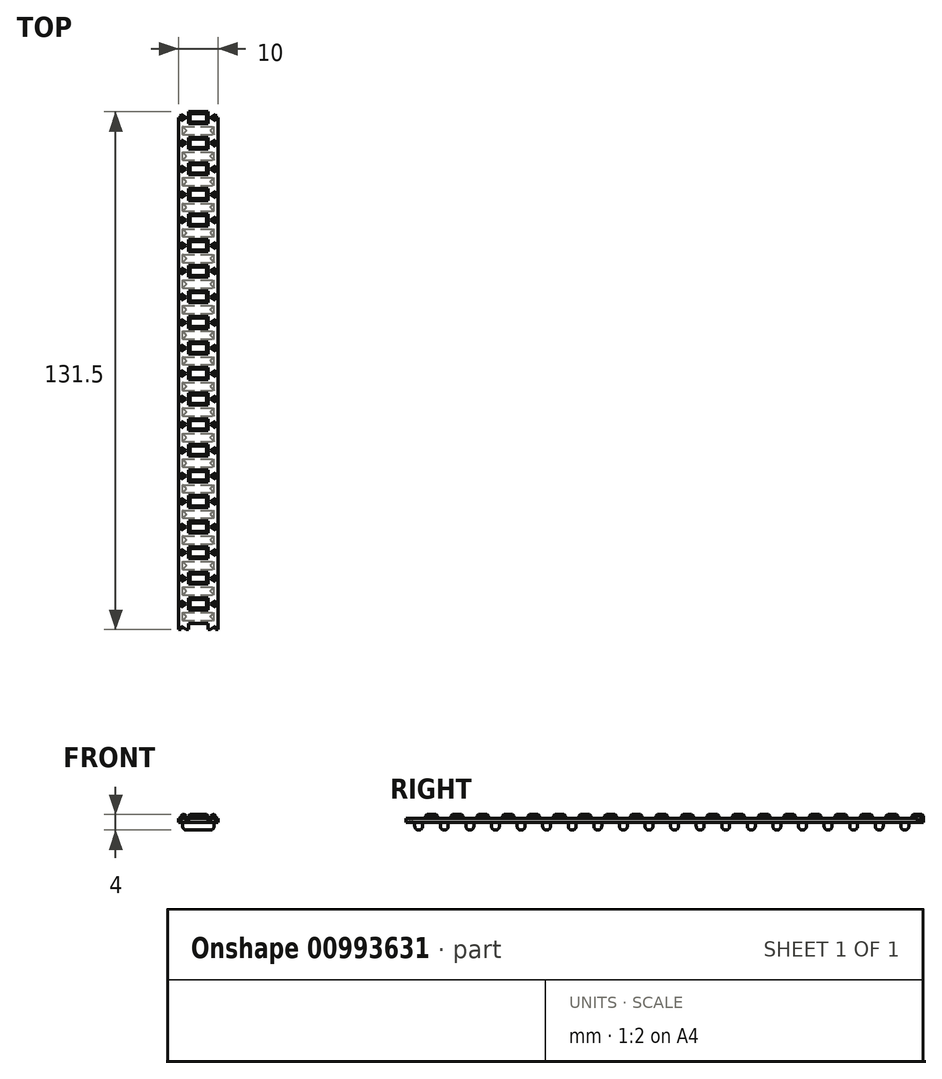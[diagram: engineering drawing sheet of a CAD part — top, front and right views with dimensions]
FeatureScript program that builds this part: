
annotation { "Feature Type Name" : "Feature", "Feature Type Description" : "" }
export const myFeature = defineFeature(function(context is Context, id is Id, definition is map)
    precondition{}
    {
        {
            var Q0;
            Q0=qCreatedBy(makeId("Top.planeOp"),FACE);
            var sketch = newSketch(context, id + "F0", { "sketchPlane" : qUnion([Q0])});
            skLineSegment(sketch, "E0.bottom", {"start": v(5, 65) * mm, "end": v(-5, 65) * mm});
            skLineSegment(sketch, "E0.top", {"start": v(5, -65) * mm, "end": v(-5, -65) * mm});
            skLineSegment(sketch, "E0.left", {"start": v(5, 65) * mm, "end": v(5, -65) * mm});
            skLineSegment(sketch, "E0.right", {"start": v(-5, 65) * mm, "end": v(-5, -65) * mm});
            skPoint(sketch, "E0.middle", {"position": v(0, 0) * mm});
            skLineSegment(sketch, "E1.bottom", {"start": v(2.5, 1.5) * mm, "end": v(-2.5, 1.5) * mm});
            skLineSegment(sketch, "E1.top", {"start": v(2.5, -1.5) * mm, "end": v(-2.5, -1.5) * mm});
            skLineSegment(sketch, "E1.left", {"start": v(2.5, 1.5) * mm, "end": v(2.5, -1.5) * mm});
            skLineSegment(sketch, "E1.right", {"start": v(-2.5, 1.5) * mm, "end": v(-2.5, -1.5) * mm});
            skLineSegment(sketch, "E2", {"start": v(3.08, 0) * mm, "end": v(4.42, 0.87) * mm});
            skLineSegment(sketch, "E3", {"start": v(4.42, 0.87) * mm, "end": v(4.42, 0) * mm});
            skLineSegment(sketch, "E4", {"start": v(4.42, 0) * mm, "end": v(3.08, 0) * mm});
            skLineSegment(sketch, "E5", {"start": v(3.08, 0) * mm, "end": v(4.42, -0.87) * mm});
            skLineSegment(sketch, "E6", {"start": v(4.42, -0.87) * mm, "end": v(4.42, 0) * mm});
            skLineSegment(sketch, "E7", {"start": v(4.42, 0) * mm, "end": v(5, 0) * mm});
            skLineSegment(sketch, "E8", {"start": v(3.08, 0) * mm, "end": v(2.5, 0) * mm});
            skLineSegment(sketch, "E9.MirrorCS", {"start": v(-3.08, 0) * mm, "end": v(-4.42, 0.87) * mm});
            skLineSegment(sketch, "E10.MirrorCS", {"start": v(-3.08, 0) * mm, "end": v(-4.42, -0.87) * mm});
            skLineSegment(sketch, "E11.MirrorCS", {"start": v(-4.42, -0.87) * mm, "end": v(-4.42, 0) * mm});
            skLineSegment(sketch, "E12.MirrorCS", {"start": v(-4.42, 0.87) * mm, "end": v(-4.42, 0) * mm});
            skLineSegment(sketch, "E13.0.1.0", {"start": v(3.08, 6.5) * mm, "end": v(4.42, 7.37) * mm});
            skLineSegment(sketch, "E13.0.1.1", {"start": v(4.42, 7.37) * mm, "end": v(4.42, 6.5) * mm});
            skLineSegment(sketch, "E13.0.1.2", {"start": v(4.42, 5.63) * mm, "end": v(4.42, 6.5) * mm});
            skLineSegment(sketch, "E13.0.1.3", {"start": v(3.08, 6.5) * mm, "end": v(4.42, 5.63) * mm});
            skLineSegment(sketch, "E13.0.1.4", {"start": v(-4.42, 7.37) * mm, "end": v(-4.42, 6.5) * mm});
            skLineSegment(sketch, "E13.0.1.5", {"start": v(-3.08, 6.5) * mm, "end": v(-4.42, 7.37) * mm});
            skLineSegment(sketch, "E13.0.1.6", {"start": v(-3.08, 6.5) * mm, "end": v(-4.42, 5.63) * mm});
            skLineSegment(sketch, "E13.0.1.7", {"start": v(-4.42, 5.63) * mm, "end": v(-4.42, 6.5) * mm});
            skLineSegment(sketch, "E13.0.1.8", {"start": v(2.5, 8) * mm, "end": v(-2.5, 8) * mm});
            skLineSegment(sketch, "E13.0.1.9", {"start": v(-2.5, 8) * mm, "end": v(-2.5, 5) * mm});
            skLineSegment(sketch, "E13.0.1.10", {"start": v(2.5, 5) * mm, "end": v(-2.5, 5) * mm});
            skLineSegment(sketch, "E13.0.1.11", {"start": v(2.5, 8) * mm, "end": v(2.5, 5) * mm});
            skLineSegment(sketch, "E13.0.2.0", {"start": v(3.08, 13) * mm, "end": v(4.42, 13.87) * mm});
            skLineSegment(sketch, "E13.0.2.1", {"start": v(4.42, 13.87) * mm, "end": v(4.42, 13) * mm});
            skLineSegment(sketch, "E13.0.2.2", {"start": v(4.42, 12.13) * mm, "end": v(4.42, 13) * mm});
            skLineSegment(sketch, "E13.0.2.3", {"start": v(3.08, 13) * mm, "end": v(4.42, 12.13) * mm});
            skLineSegment(sketch, "E13.0.2.4", {"start": v(-4.42, 13.87) * mm, "end": v(-4.42, 13) * mm});
            skLineSegment(sketch, "E13.0.2.5", {"start": v(-3.08, 13) * mm, "end": v(-4.42, 13.87) * mm});
            skLineSegment(sketch, "E13.0.2.6", {"start": v(-3.08, 13) * mm, "end": v(-4.42, 12.13) * mm});
            skLineSegment(sketch, "E13.0.2.7", {"start": v(-4.42, 12.13) * mm, "end": v(-4.42, 13) * mm});
            skLineSegment(sketch, "E13.0.2.8", {"start": v(2.5, 14.5) * mm, "end": v(-2.5, 14.5) * mm});
            skLineSegment(sketch, "E13.0.2.9", {"start": v(-2.5, 14.5) * mm, "end": v(-2.5, 11.5) * mm});
            skLineSegment(sketch, "E13.0.2.10", {"start": v(2.5, 11.5) * mm, "end": v(-2.5, 11.5) * mm});
            skLineSegment(sketch, "E13.0.2.11", {"start": v(2.5, 14.5) * mm, "end": v(2.5, 11.5) * mm});
            skLineSegment(sketch, "E13.0.3.0", {"start": v(3.08, 19.5) * mm, "end": v(4.42, 20.37) * mm});
            skLineSegment(sketch, "E13.0.3.1", {"start": v(4.42, 20.37) * mm, "end": v(4.42, 19.5) * mm});
            skLineSegment(sketch, "E13.0.3.2", {"start": v(4.42, 18.63) * mm, "end": v(4.42, 19.5) * mm});
            skLineSegment(sketch, "E13.0.3.3", {"start": v(3.08, 19.5) * mm, "end": v(4.42, 18.63) * mm});
            skLineSegment(sketch, "E13.0.3.4", {"start": v(-4.42, 20.37) * mm, "end": v(-4.42, 19.5) * mm});
            skLineSegment(sketch, "E13.0.3.5", {"start": v(-3.08, 19.5) * mm, "end": v(-4.42, 20.37) * mm});
            skLineSegment(sketch, "E13.0.3.6", {"start": v(-3.08, 19.5) * mm, "end": v(-4.42, 18.63) * mm});
            skLineSegment(sketch, "E13.0.3.7", {"start": v(-4.42, 18.63) * mm, "end": v(-4.42, 19.5) * mm});
            skLineSegment(sketch, "E13.0.3.8", {"start": v(2.5, 21) * mm, "end": v(-2.5, 21) * mm});
            skLineSegment(sketch, "E13.0.3.9", {"start": v(-2.5, 21) * mm, "end": v(-2.5, 18) * mm});
            skLineSegment(sketch, "E13.0.3.10", {"start": v(2.5, 18) * mm, "end": v(-2.5, 18) * mm});
            skLineSegment(sketch, "E13.0.3.11", {"start": v(2.5, 21) * mm, "end": v(2.5, 18) * mm});
            skLineSegment(sketch, "E13.0.4.0", {"start": v(3.08, 26) * mm, "end": v(4.42, 26.87) * mm});
            skLineSegment(sketch, "E13.0.4.1", {"start": v(4.42, 26.87) * mm, "end": v(4.42, 26) * mm});
            skLineSegment(sketch, "E13.0.4.2", {"start": v(4.42, 25.13) * mm, "end": v(4.42, 26) * mm});
            skLineSegment(sketch, "E13.0.4.3", {"start": v(3.08, 26) * mm, "end": v(4.42, 25.13) * mm});
            skLineSegment(sketch, "E13.0.4.4", {"start": v(-4.42, 26.87) * mm, "end": v(-4.42, 26) * mm});
            skLineSegment(sketch, "E13.0.4.5", {"start": v(-3.08, 26) * mm, "end": v(-4.42, 26.87) * mm});
            skLineSegment(sketch, "E13.0.4.6", {"start": v(-3.08, 26) * mm, "end": v(-4.42, 25.13) * mm});
            skLineSegment(sketch, "E13.0.4.7", {"start": v(-4.42, 25.13) * mm, "end": v(-4.42, 26) * mm});
            skLineSegment(sketch, "E13.0.4.8", {"start": v(2.5, 27.5) * mm, "end": v(-2.5, 27.5) * mm});
            skLineSegment(sketch, "E13.0.4.9", {"start": v(-2.5, 27.5) * mm, "end": v(-2.5, 24.5) * mm});
            skLineSegment(sketch, "E13.0.4.10", {"start": v(2.5, 24.5) * mm, "end": v(-2.5, 24.5) * mm});
            skLineSegment(sketch, "E13.0.4.11", {"start": v(2.5, 27.5) * mm, "end": v(2.5, 24.5) * mm});
            skLineSegment(sketch, "E13.0.5.0", {"start": v(3.08, 32.5) * mm, "end": v(4.42, 33.37) * mm});
            skLineSegment(sketch, "E13.0.5.1", {"start": v(4.42, 33.37) * mm, "end": v(4.42, 32.5) * mm});
            skLineSegment(sketch, "E13.0.5.2", {"start": v(4.42, 31.63) * mm, "end": v(4.42, 32.5) * mm});
            skLineSegment(sketch, "E13.0.5.3", {"start": v(3.08, 32.5) * mm, "end": v(4.42, 31.63) * mm});
            skLineSegment(sketch, "E13.0.5.4", {"start": v(-4.42, 33.37) * mm, "end": v(-4.42, 32.5) * mm});
            skLineSegment(sketch, "E13.0.5.5", {"start": v(-3.08, 32.5) * mm, "end": v(-4.42, 33.37) * mm});
            skLineSegment(sketch, "E13.0.5.6", {"start": v(-3.08, 32.5) * mm, "end": v(-4.42, 31.63) * mm});
            skLineSegment(sketch, "E13.0.5.7", {"start": v(-4.42, 31.63) * mm, "end": v(-4.42, 32.5) * mm});
            skLineSegment(sketch, "E13.0.5.8", {"start": v(2.5, 34) * mm, "end": v(-2.5, 34) * mm});
            skLineSegment(sketch, "E13.0.5.9", {"start": v(-2.5, 34) * mm, "end": v(-2.5, 31) * mm});
            skLineSegment(sketch, "E13.0.5.10", {"start": v(2.5, 31) * mm, "end": v(-2.5, 31) * mm});
            skLineSegment(sketch, "E13.0.5.11", {"start": v(2.5, 34) * mm, "end": v(2.5, 31) * mm});
            skLineSegment(sketch, "E13.0.6.0", {"start": v(3.08, 39) * mm, "end": v(4.42, 39.87) * mm});
            skLineSegment(sketch, "E13.0.6.1", {"start": v(4.42, 39.87) * mm, "end": v(4.42, 39) * mm});
            skLineSegment(sketch, "E13.0.6.2", {"start": v(4.42, 38.13) * mm, "end": v(4.42, 39) * mm});
            skLineSegment(sketch, "E13.0.6.3", {"start": v(3.08, 39) * mm, "end": v(4.42, 38.13) * mm});
            skLineSegment(sketch, "E13.0.6.4", {"start": v(-4.42, 39.87) * mm, "end": v(-4.42, 39) * mm});
            skLineSegment(sketch, "E13.0.6.5", {"start": v(-3.08, 39) * mm, "end": v(-4.42, 39.87) * mm});
            skLineSegment(sketch, "E13.0.6.6", {"start": v(-3.08, 39) * mm, "end": v(-4.42, 38.13) * mm});
            skLineSegment(sketch, "E13.0.6.7", {"start": v(-4.42, 38.13) * mm, "end": v(-4.42, 39) * mm});
            skLineSegment(sketch, "E13.0.6.8", {"start": v(2.5, 40.5) * mm, "end": v(-2.5, 40.5) * mm});
            skLineSegment(sketch, "E13.0.6.9", {"start": v(-2.5, 40.5) * mm, "end": v(-2.5, 37.5) * mm});
            skLineSegment(sketch, "E13.0.6.10", {"start": v(2.5, 37.5) * mm, "end": v(-2.5, 37.5) * mm});
            skLineSegment(sketch, "E13.0.6.11", {"start": v(2.5, 40.5) * mm, "end": v(2.5, 37.5) * mm});
            skLineSegment(sketch, "E13.0.7.0", {"start": v(3.08, 45.5) * mm, "end": v(4.42, 46.37) * mm});
            skLineSegment(sketch, "E13.0.7.1", {"start": v(4.42, 46.37) * mm, "end": v(4.42, 45.5) * mm});
            skLineSegment(sketch, "E13.0.7.2", {"start": v(4.42, 44.63) * mm, "end": v(4.42, 45.5) * mm});
            skLineSegment(sketch, "E13.0.7.3", {"start": v(3.08, 45.5) * mm, "end": v(4.42, 44.63) * mm});
            skLineSegment(sketch, "E13.0.7.4", {"start": v(-4.42, 46.37) * mm, "end": v(-4.42, 45.5) * mm});
            skLineSegment(sketch, "E13.0.7.5", {"start": v(-3.08, 45.5) * mm, "end": v(-4.42, 46.37) * mm});
            skLineSegment(sketch, "E13.0.7.6", {"start": v(-3.08, 45.5) * mm, "end": v(-4.42, 44.63) * mm});
            skLineSegment(sketch, "E13.0.7.7", {"start": v(-4.42, 44.63) * mm, "end": v(-4.42, 45.5) * mm});
            skLineSegment(sketch, "E13.0.7.8", {"start": v(2.5, 47) * mm, "end": v(-2.5, 47) * mm});
            skLineSegment(sketch, "E13.0.7.9", {"start": v(-2.5, 47) * mm, "end": v(-2.5, 44) * mm});
            skLineSegment(sketch, "E13.0.7.10", {"start": v(2.5, 44) * mm, "end": v(-2.5, 44) * mm});
            skLineSegment(sketch, "E13.0.7.11", {"start": v(2.5, 47) * mm, "end": v(2.5, 44) * mm});
            skLineSegment(sketch, "E13.0.8.0", {"start": v(3.08, 52) * mm, "end": v(4.42, 52.87) * mm});
            skLineSegment(sketch, "E13.0.8.1", {"start": v(4.42, 52.87) * mm, "end": v(4.42, 52) * mm});
            skLineSegment(sketch, "E13.0.8.2", {"start": v(4.42, 51.13) * mm, "end": v(4.42, 52) * mm});
            skLineSegment(sketch, "E13.0.8.3", {"start": v(3.08, 52) * mm, "end": v(4.42, 51.13) * mm});
            skLineSegment(sketch, "E13.0.8.4", {"start": v(-4.42, 52.87) * mm, "end": v(-4.42, 52) * mm});
            skLineSegment(sketch, "E13.0.8.5", {"start": v(-3.08, 52) * mm, "end": v(-4.42, 52.87) * mm});
            skLineSegment(sketch, "E13.0.8.6", {"start": v(-3.08, 52) * mm, "end": v(-4.42, 51.13) * mm});
            skLineSegment(sketch, "E13.0.8.7", {"start": v(-4.42, 51.13) * mm, "end": v(-4.42, 52) * mm});
            skLineSegment(sketch, "E13.0.8.8", {"start": v(2.5, 53.5) * mm, "end": v(-2.5, 53.5) * mm});
            skLineSegment(sketch, "E13.0.8.9", {"start": v(-2.5, 53.5) * mm, "end": v(-2.5, 50.5) * mm});
            skLineSegment(sketch, "E13.0.8.10", {"start": v(2.5, 50.5) * mm, "end": v(-2.5, 50.5) * mm});
            skLineSegment(sketch, "E13.0.8.11", {"start": v(2.5, 53.5) * mm, "end": v(2.5, 50.5) * mm});
            skLineSegment(sketch, "E13.0.9.0", {"start": v(3.08, 58.5) * mm, "end": v(4.42, 59.37) * mm});
            skLineSegment(sketch, "E13.0.9.1", {"start": v(4.42, 59.37) * mm, "end": v(4.42, 58.5) * mm});
            skLineSegment(sketch, "E13.0.9.2", {"start": v(4.42, 57.63) * mm, "end": v(4.42, 58.5) * mm});
            skLineSegment(sketch, "E13.0.9.3", {"start": v(3.08, 58.5) * mm, "end": v(4.42, 57.63) * mm});
            skLineSegment(sketch, "E13.0.9.4", {"start": v(-4.42, 59.37) * mm, "end": v(-4.42, 58.5) * mm});
            skLineSegment(sketch, "E13.0.9.5", {"start": v(-3.08, 58.5) * mm, "end": v(-4.42, 59.37) * mm});
            skLineSegment(sketch, "E13.0.9.6", {"start": v(-3.08, 58.5) * mm, "end": v(-4.42, 57.63) * mm});
            skLineSegment(sketch, "E13.0.9.7", {"start": v(-4.42, 57.63) * mm, "end": v(-4.42, 58.5) * mm});
            skLineSegment(sketch, "E13.0.9.8", {"start": v(2.5, 60) * mm, "end": v(-2.5, 60) * mm});
            skLineSegment(sketch, "E13.0.9.9", {"start": v(-2.5, 60) * mm, "end": v(-2.5, 57) * mm});
            skLineSegment(sketch, "E13.0.9.10", {"start": v(2.5, 57) * mm, "end": v(-2.5, 57) * mm});
            skLineSegment(sketch, "E13.0.9.11", {"start": v(2.5, 60) * mm, "end": v(2.5, 57) * mm});
            skLineSegment(sketch, "E13.0.10.0", {"start": v(3.08, 65) * mm, "end": v(4.42, 65.87) * mm});
            skLineSegment(sketch, "E13.0.10.1", {"start": v(4.42, 65.87) * mm, "end": v(4.42, 65) * mm});
            skLineSegment(sketch, "E13.0.10.2", {"start": v(4.42, 64.13) * mm, "end": v(4.42, 65) * mm});
            skLineSegment(sketch, "E13.0.10.3", {"start": v(3.08, 65) * mm, "end": v(4.42, 64.13) * mm});
            skLineSegment(sketch, "E13.0.10.4", {"start": v(-4.42, 65.87) * mm, "end": v(-4.42, 65) * mm});
            skLineSegment(sketch, "E13.0.10.5", {"start": v(-3.08, 65) * mm, "end": v(-4.42, 65.87) * mm});
            skLineSegment(sketch, "E13.0.10.6", {"start": v(-3.08, 65) * mm, "end": v(-4.42, 64.13) * mm});
            skLineSegment(sketch, "E13.0.10.7", {"start": v(-4.42, 64.13) * mm, "end": v(-4.42, 65) * mm});
            skLineSegment(sketch, "E13.0.10.8", {"start": v(2.5, 66.5) * mm, "end": v(-2.5, 66.5) * mm});
            skLineSegment(sketch, "E13.0.10.9", {"start": v(-2.5, 66.5) * mm, "end": v(-2.5, 63.5) * mm});
            skLineSegment(sketch, "E13.0.10.10", {"start": v(2.5, 63.5) * mm, "end": v(-2.5, 63.5) * mm});
            skLineSegment(sketch, "E13.0.10.11", {"start": v(2.5, 66.5) * mm, "end": v(2.5, 63.5) * mm});
            skLineSegment(sketch, "E13.direction1", {"start": v(3.08, 0) * mm, "end": v(20.08, 0) * mm, "construction": true});
            skLineSegment(sketch, "E13.direction2", {"start": v(3.08, 0) * mm, "end": v(3.08, 6.5) * mm, "construction": true});
            skLineSegment(sketch, "E14.0.1.0", {"start": v(-3.08, -6.5) * mm, "end": v(-4.42, -5.63) * mm});
            skLineSegment(sketch, "E14.0.1.1", {"start": v(-4.42, -5.63) * mm, "end": v(-4.42, -6.5) * mm});
            skLineSegment(sketch, "E14.0.1.2", {"start": v(-4.42, -7.37) * mm, "end": v(-4.42, -6.5) * mm});
            skLineSegment(sketch, "E14.0.1.3", {"start": v(-3.08, -6.5) * mm, "end": v(-4.42, -7.37) * mm});
            skLineSegment(sketch, "E14.0.1.4", {"start": v(-2.5, -5) * mm, "end": v(-2.5, -8) * mm});
            skLineSegment(sketch, "E14.0.1.5", {"start": v(2.5, -5) * mm, "end": v(-2.5, -5) * mm});
            skLineSegment(sketch, "E14.0.1.6", {"start": v(2.5, -5) * mm, "end": v(2.5, -8) * mm});
            skLineSegment(sketch, "E14.0.1.7", {"start": v(2.5, -8) * mm, "end": v(-2.5, -8) * mm});
            skLineSegment(sketch, "E14.0.1.8", {"start": v(3.08, -6.5) * mm, "end": v(4.42, -7.37) * mm});
            skLineSegment(sketch, "E14.0.1.9", {"start": v(3.08, -6.5) * mm, "end": v(4.42, -5.63) * mm});
            skLineSegment(sketch, "E14.0.1.10", {"start": v(4.42, -5.63) * mm, "end": v(4.42, -6.5) * mm});
            skLineSegment(sketch, "E14.0.1.11", {"start": v(4.42, -7.37) * mm, "end": v(4.42, -6.5) * mm});
            skLineSegment(sketch, "E14.0.2.0", {"start": v(-3.08, -13) * mm, "end": v(-4.42, -12.13) * mm});
            skLineSegment(sketch, "E14.0.2.1", {"start": v(-4.42, -12.13) * mm, "end": v(-4.42, -13) * mm});
            skLineSegment(sketch, "E14.0.2.2", {"start": v(-4.42, -13.87) * mm, "end": v(-4.42, -13) * mm});
            skLineSegment(sketch, "E14.0.2.3", {"start": v(-3.08, -13) * mm, "end": v(-4.42, -13.87) * mm});
            skLineSegment(sketch, "E14.0.2.4", {"start": v(-2.5, -11.5) * mm, "end": v(-2.5, -14.5) * mm});
            skLineSegment(sketch, "E14.0.2.5", {"start": v(2.5, -11.5) * mm, "end": v(-2.5, -11.5) * mm});
            skLineSegment(sketch, "E14.0.2.6", {"start": v(2.5, -11.5) * mm, "end": v(2.5, -14.5) * mm});
            skLineSegment(sketch, "E14.0.2.7", {"start": v(2.5, -14.5) * mm, "end": v(-2.5, -14.5) * mm});
            skLineSegment(sketch, "E14.0.2.8", {"start": v(3.08, -13) * mm, "end": v(4.42, -13.87) * mm});
            skLineSegment(sketch, "E14.0.2.9", {"start": v(3.08, -13) * mm, "end": v(4.42, -12.13) * mm});
            skLineSegment(sketch, "E14.0.2.10", {"start": v(4.42, -12.13) * mm, "end": v(4.42, -13) * mm});
            skLineSegment(sketch, "E14.0.2.11", {"start": v(4.42, -13.87) * mm, "end": v(4.42, -13) * mm});
            skLineSegment(sketch, "E14.0.3.0", {"start": v(-3.08, -19.5) * mm, "end": v(-4.42, -18.63) * mm});
            skLineSegment(sketch, "E14.0.3.1", {"start": v(-4.42, -18.63) * mm, "end": v(-4.42, -19.5) * mm});
            skLineSegment(sketch, "E14.0.3.2", {"start": v(-4.42, -20.37) * mm, "end": v(-4.42, -19.5) * mm});
            skLineSegment(sketch, "E14.0.3.3", {"start": v(-3.08, -19.5) * mm, "end": v(-4.42, -20.37) * mm});
            skLineSegment(sketch, "E14.0.3.4", {"start": v(-2.5, -18) * mm, "end": v(-2.5, -21) * mm});
            skLineSegment(sketch, "E14.0.3.5", {"start": v(2.5, -18) * mm, "end": v(-2.5, -18) * mm});
            skLineSegment(sketch, "E14.0.3.6", {"start": v(2.5, -18) * mm, "end": v(2.5, -21) * mm});
            skLineSegment(sketch, "E14.0.3.7", {"start": v(2.5, -21) * mm, "end": v(-2.5, -21) * mm});
            skLineSegment(sketch, "E14.0.3.8", {"start": v(3.08, -19.5) * mm, "end": v(4.42, -20.37) * mm});
            skLineSegment(sketch, "E14.0.3.9", {"start": v(3.08, -19.5) * mm, "end": v(4.42, -18.63) * mm});
            skLineSegment(sketch, "E14.0.3.10", {"start": v(4.42, -18.63) * mm, "end": v(4.42, -19.5) * mm});
            skLineSegment(sketch, "E14.0.3.11", {"start": v(4.42, -20.37) * mm, "end": v(4.42, -19.5) * mm});
            skLineSegment(sketch, "E14.0.4.0", {"start": v(-3.08, -26) * mm, "end": v(-4.42, -25.13) * mm});
            skLineSegment(sketch, "E14.0.4.1", {"start": v(-4.42, -25.13) * mm, "end": v(-4.42, -26) * mm});
            skLineSegment(sketch, "E14.0.4.2", {"start": v(-4.42, -26.87) * mm, "end": v(-4.42, -26) * mm});
            skLineSegment(sketch, "E14.0.4.3", {"start": v(-3.08, -26) * mm, "end": v(-4.42, -26.87) * mm});
            skLineSegment(sketch, "E14.0.4.4", {"start": v(-2.5, -24.5) * mm, "end": v(-2.5, -27.5) * mm});
            skLineSegment(sketch, "E14.0.4.5", {"start": v(2.5, -24.5) * mm, "end": v(-2.5, -24.5) * mm});
            skLineSegment(sketch, "E14.0.4.6", {"start": v(2.5, -24.5) * mm, "end": v(2.5, -27.5) * mm});
            skLineSegment(sketch, "E14.0.4.7", {"start": v(2.5, -27.5) * mm, "end": v(-2.5, -27.5) * mm});
            skLineSegment(sketch, "E14.0.4.8", {"start": v(3.08, -26) * mm, "end": v(4.42, -26.87) * mm});
            skLineSegment(sketch, "E14.0.4.9", {"start": v(3.08, -26) * mm, "end": v(4.42, -25.13) * mm});
            skLineSegment(sketch, "E14.0.4.10", {"start": v(4.42, -25.13) * mm, "end": v(4.42, -26) * mm});
            skLineSegment(sketch, "E14.0.4.11", {"start": v(4.42, -26.87) * mm, "end": v(4.42, -26) * mm});
            skLineSegment(sketch, "E14.0.5.0", {"start": v(-3.08, -32.5) * mm, "end": v(-4.42, -31.63) * mm});
            skLineSegment(sketch, "E14.0.5.1", {"start": v(-4.42, -31.63) * mm, "end": v(-4.42, -32.5) * mm});
            skLineSegment(sketch, "E14.0.5.2", {"start": v(-4.42, -33.37) * mm, "end": v(-4.42, -32.5) * mm});
            skLineSegment(sketch, "E14.0.5.3", {"start": v(-3.08, -32.5) * mm, "end": v(-4.42, -33.37) * mm});
            skLineSegment(sketch, "E14.0.5.4", {"start": v(-2.5, -31) * mm, "end": v(-2.5, -34) * mm});
            skLineSegment(sketch, "E14.0.5.5", {"start": v(2.5, -31) * mm, "end": v(-2.5, -31) * mm});
            skLineSegment(sketch, "E14.0.5.6", {"start": v(2.5, -31) * mm, "end": v(2.5, -34) * mm});
            skLineSegment(sketch, "E14.0.5.7", {"start": v(2.5, -34) * mm, "end": v(-2.5, -34) * mm});
            skLineSegment(sketch, "E14.0.5.8", {"start": v(3.08, -32.5) * mm, "end": v(4.42, -33.37) * mm});
            skLineSegment(sketch, "E14.0.5.9", {"start": v(3.08, -32.5) * mm, "end": v(4.42, -31.63) * mm});
            skLineSegment(sketch, "E14.0.5.10", {"start": v(4.42, -31.63) * mm, "end": v(4.42, -32.5) * mm});
            skLineSegment(sketch, "E14.0.5.11", {"start": v(4.42, -33.37) * mm, "end": v(4.42, -32.5) * mm});
            skLineSegment(sketch, "E14.0.6.0", {"start": v(-3.08, -39) * mm, "end": v(-4.42, -38.13) * mm});
            skLineSegment(sketch, "E14.0.6.1", {"start": v(-4.42, -38.13) * mm, "end": v(-4.42, -39) * mm});
            skLineSegment(sketch, "E14.0.6.2", {"start": v(-4.42, -39.87) * mm, "end": v(-4.42, -39) * mm});
            skLineSegment(sketch, "E14.0.6.3", {"start": v(-3.08, -39) * mm, "end": v(-4.42, -39.87) * mm});
            skLineSegment(sketch, "E14.0.6.4", {"start": v(-2.5, -37.5) * mm, "end": v(-2.5, -40.5) * mm});
            skLineSegment(sketch, "E14.0.6.5", {"start": v(2.5, -37.5) * mm, "end": v(-2.5, -37.5) * mm});
            skLineSegment(sketch, "E14.0.6.6", {"start": v(2.5, -37.5) * mm, "end": v(2.5, -40.5) * mm});
            skLineSegment(sketch, "E14.0.6.7", {"start": v(2.5, -40.5) * mm, "end": v(-2.5, -40.5) * mm});
            skLineSegment(sketch, "E14.0.6.8", {"start": v(3.08, -39) * mm, "end": v(4.42, -39.87) * mm});
            skLineSegment(sketch, "E14.0.6.9", {"start": v(3.08, -39) * mm, "end": v(4.42, -38.13) * mm});
            skLineSegment(sketch, "E14.0.6.10", {"start": v(4.42, -38.13) * mm, "end": v(4.42, -39) * mm});
            skLineSegment(sketch, "E14.0.6.11", {"start": v(4.42, -39.87) * mm, "end": v(4.42, -39) * mm});
            skLineSegment(sketch, "E14.0.7.0", {"start": v(-3.08, -45.5) * mm, "end": v(-4.42, -44.63) * mm});
            skLineSegment(sketch, "E14.0.7.1", {"start": v(-4.42, -44.63) * mm, "end": v(-4.42, -45.5) * mm});
            skLineSegment(sketch, "E14.0.7.2", {"start": v(-4.42, -46.37) * mm, "end": v(-4.42, -45.5) * mm});
            skLineSegment(sketch, "E14.0.7.3", {"start": v(-3.08, -45.5) * mm, "end": v(-4.42, -46.37) * mm});
            skLineSegment(sketch, "E14.0.7.4", {"start": v(-2.5, -44) * mm, "end": v(-2.5, -47) * mm});
            skLineSegment(sketch, "E14.0.7.5", {"start": v(2.5, -44) * mm, "end": v(-2.5, -44) * mm});
            skLineSegment(sketch, "E14.0.7.6", {"start": v(2.5, -44) * mm, "end": v(2.5, -47) * mm});
            skLineSegment(sketch, "E14.0.7.7", {"start": v(2.5, -47) * mm, "end": v(-2.5, -47) * mm});
            skLineSegment(sketch, "E14.0.7.8", {"start": v(3.08, -45.5) * mm, "end": v(4.42, -46.37) * mm});
            skLineSegment(sketch, "E14.0.7.9", {"start": v(3.08, -45.5) * mm, "end": v(4.42, -44.63) * mm});
            skLineSegment(sketch, "E14.0.7.10", {"start": v(4.42, -44.63) * mm, "end": v(4.42, -45.5) * mm});
            skLineSegment(sketch, "E14.0.7.11", {"start": v(4.42, -46.37) * mm, "end": v(4.42, -45.5) * mm});
            skLineSegment(sketch, "E14.0.8.0", {"start": v(-3.08, -52) * mm, "end": v(-4.42, -51.13) * mm});
            skLineSegment(sketch, "E14.0.8.1", {"start": v(-4.42, -51.13) * mm, "end": v(-4.42, -52) * mm});
            skLineSegment(sketch, "E14.0.8.2", {"start": v(-4.42, -52.87) * mm, "end": v(-4.42, -52) * mm});
            skLineSegment(sketch, "E14.0.8.3", {"start": v(-3.08, -52) * mm, "end": v(-4.42, -52.87) * mm});
            skLineSegment(sketch, "E14.0.8.4", {"start": v(-2.5, -50.5) * mm, "end": v(-2.5, -53.5) * mm});
            skLineSegment(sketch, "E14.0.8.5", {"start": v(2.5, -50.5) * mm, "end": v(-2.5, -50.5) * mm});
            skLineSegment(sketch, "E14.0.8.6", {"start": v(2.5, -50.5) * mm, "end": v(2.5, -53.5) * mm});
            skLineSegment(sketch, "E14.0.8.7", {"start": v(2.5, -53.5) * mm, "end": v(-2.5, -53.5) * mm});
            skLineSegment(sketch, "E14.0.8.8", {"start": v(3.08, -52) * mm, "end": v(4.42, -52.87) * mm});
            skLineSegment(sketch, "E14.0.8.9", {"start": v(3.08, -52) * mm, "end": v(4.42, -51.13) * mm});
            skLineSegment(sketch, "E14.0.8.10", {"start": v(4.42, -51.13) * mm, "end": v(4.42, -52) * mm});
            skLineSegment(sketch, "E14.0.8.11", {"start": v(4.42, -52.87) * mm, "end": v(4.42, -52) * mm});
            skLineSegment(sketch, "E14.0.9.0", {"start": v(-3.08, -58.5) * mm, "end": v(-4.42, -57.63) * mm});
            skLineSegment(sketch, "E14.0.9.1", {"start": v(-4.42, -57.63) * mm, "end": v(-4.42, -58.5) * mm});
            skLineSegment(sketch, "E14.0.9.2", {"start": v(-4.42, -59.37) * mm, "end": v(-4.42, -58.5) * mm});
            skLineSegment(sketch, "E14.0.9.3", {"start": v(-3.08, -58.5) * mm, "end": v(-4.42, -59.37) * mm});
            skLineSegment(sketch, "E14.0.9.4", {"start": v(-2.5, -57) * mm, "end": v(-2.5, -60) * mm});
            skLineSegment(sketch, "E14.0.9.5", {"start": v(2.5, -57) * mm, "end": v(-2.5, -57) * mm});
            skLineSegment(sketch, "E14.0.9.6", {"start": v(2.5, -57) * mm, "end": v(2.5, -60) * mm});
            skLineSegment(sketch, "E14.0.9.7", {"start": v(2.5, -60) * mm, "end": v(-2.5, -60) * mm});
            skLineSegment(sketch, "E14.0.9.8", {"start": v(3.08, -58.5) * mm, "end": v(4.42, -59.37) * mm});
            skLineSegment(sketch, "E14.0.9.9", {"start": v(3.08, -58.5) * mm, "end": v(4.42, -57.63) * mm});
            skLineSegment(sketch, "E14.0.9.10", {"start": v(4.42, -57.63) * mm, "end": v(4.42, -58.5) * mm});
            skLineSegment(sketch, "E14.0.9.11", {"start": v(4.42, -59.37) * mm, "end": v(4.42, -58.5) * mm});
            skLineSegment(sketch, "E14.0.10.0", {"start": v(-3.08, -65) * mm, "end": v(-4.42, -64.13) * mm});
            skLineSegment(sketch, "E14.0.10.1", {"start": v(-4.42, -64.13) * mm, "end": v(-4.42, -65) * mm});
            skLineSegment(sketch, "E14.0.10.2", {"start": v(-4.42, -65.87) * mm, "end": v(-4.42, -65) * mm});
            skLineSegment(sketch, "E14.0.10.3", {"start": v(-3.08, -65) * mm, "end": v(-4.42, -65.87) * mm});
            skLineSegment(sketch, "E14.0.10.4", {"start": v(-2.5, -63.5) * mm, "end": v(-2.5, -66.5) * mm});
            skLineSegment(sketch, "E14.0.10.5", {"start": v(2.5, -63.5) * mm, "end": v(-2.5, -63.5) * mm});
            skLineSegment(sketch, "E14.0.10.6", {"start": v(2.5, -63.5) * mm, "end": v(2.5, -66.5) * mm});
            skLineSegment(sketch, "E14.0.10.7", {"start": v(2.5, -66.5) * mm, "end": v(-2.5, -66.5) * mm});
            skLineSegment(sketch, "E14.0.10.8", {"start": v(3.08, -65) * mm, "end": v(4.42, -65.87) * mm});
            skLineSegment(sketch, "E14.0.10.9", {"start": v(3.08, -65) * mm, "end": v(4.42, -64.13) * mm});
            skLineSegment(sketch, "E14.0.10.10", {"start": v(4.42, -64.13) * mm, "end": v(4.42, -65) * mm});
            skLineSegment(sketch, "E14.0.10.11", {"start": v(4.42, -65.87) * mm, "end": v(4.42, -65) * mm});
            skLineSegment(sketch, "E14.direction1", {"start": v(-4.42, 0.87) * mm, "end": v(20.58, 0.87) * mm, "construction": true});
            skLineSegment(sketch, "E14.direction2", {"start": v(-4.42, 0.87) * mm, "end": v(-4.42, -5.63) * mm, "construction": true});
            skSolve(sketch);
        }
        {
            var Q0;
            {var subQ22=sQuery(id+"F0.wireOp",EDGE,"E0.right");Q0=makeQuery(id+"F0.imprint","IMPRINT",FACE,{"disambiguationData":[TD([[makeQuery(id+"F0.imprint","IMPRINT",EDGE,{"derivedFrom":subQ22}),1.0]])]});}
            extrude(context, id + "F1", {"entities" : qUnion([Q0]), "depth" : 1 * mm, "offsetDistance" : 25 * mm});
        }
        {
            var Q0;
            {var subQ0=sQuery(id+"F0.wireOp",EDGE,"E13.0.10.4");Q0=makeQuery(id+"F0.imprint","IMPRINT",FACE,{"disambiguationData":[TD([[makeQuery(id+"F0.imprint","IMPRINT",EDGE,{"derivedFrom":subQ0}),1.0]])]});}
            var Q1;
            {var subQ2=sQuery(id+"F0.wireOp",EDGE,"E13.0.10.6");Q1=makeQuery(id+"F0.imprint","IMPRINT",FACE,{"disambiguationData":[TD([[makeQuery(id+"F0.imprint","IMPRINT",EDGE,{"derivedFrom":subQ2}),-1.0]])]});}
            var Q2;
            {var subQ5=sQuery(id+"F0.wireOp",EDGE,"E13.0.10.8");Q2=makeQuery(id+"F0.imprint","IMPRINT",FACE,{"disambiguationData":[TD([[makeQuery(id+"F0.imprint","IMPRINT",EDGE,{"derivedFrom":subQ5}),1.0]])]});}
            var Q3;
            {var subQ5=sQuery(id+"F0.wireOp",EDGE,"E13.0.10.10");Q3=makeQuery(id+"F0.imprint","IMPRINT",FACE,{"disambiguationData":[TD([[makeQuery(id+"F0.imprint","IMPRINT",EDGE,{"derivedFrom":subQ5}),-1.0]])]});}
            var Q4;
            {var subQ0=sQuery(id+"F0.wireOp",EDGE,"E13.0.10.0");Q4=makeQuery(id+"F0.imprint","IMPRINT",FACE,{"disambiguationData":[TD([[makeQuery(id+"F0.imprint","IMPRINT",EDGE,{"derivedFrom":subQ0}),-1.0]])]});}
            var Q5;
            {var subQ2=sQuery(id+"F0.wireOp",EDGE,"E13.0.10.2");Q5=makeQuery(id+"F0.imprint","IMPRINT",FACE,{"disambiguationData":[TD([[makeQuery(id+"F0.imprint","IMPRINT",EDGE,{"derivedFrom":subQ2}),1.0]])]});}
            var Q6;
            Q6=makeQuery(id+"F0.imprint","IMPRINT",FACE,{"disambiguationData":[TD([[makeQuery(id+"F0.imprint","IMPRINT",EDGE,{"derivedFrom":sQuery(id+"F0.wireOp",EDGE,"E13.0.9.8")}),1.0]])]});
            var Q7;
            Q7=makeQuery(id+"F0.imprint","IMPRINT",FACE,{"disambiguationData":[TD([[makeQuery(id+"F0.imprint","IMPRINT",EDGE,{"derivedFrom":sQuery(id+"F0.wireOp",EDGE,"E13.0.9.0")}),-1.0]])]});
            var Q8;
            Q8=makeQuery(id+"F0.imprint","IMPRINT",FACE,{"disambiguationData":[TD([[makeQuery(id+"F0.imprint","IMPRINT",EDGE,{"derivedFrom":sQuery(id+"F0.wireOp",EDGE,"E13.0.9.4")}),1.0]])]});
            var Q9;
            Q9=makeQuery(id+"F0.imprint","IMPRINT",FACE,{"disambiguationData":[TD([[makeQuery(id+"F0.imprint","IMPRINT",EDGE,{"derivedFrom":sQuery(id+"F0.wireOp",EDGE,"E13.0.8.4")}),1.0]])]});
            var Q10;
            Q10=makeQuery(id+"F0.imprint","IMPRINT",FACE,{"disambiguationData":[TD([[makeQuery(id+"F0.imprint","IMPRINT",EDGE,{"derivedFrom":sQuery(id+"F0.wireOp",EDGE,"E13.0.8.8")}),1.0]])]});
            var Q11;
            Q11=makeQuery(id+"F0.imprint","IMPRINT",FACE,{"disambiguationData":[TD([[makeQuery(id+"F0.imprint","IMPRINT",EDGE,{"derivedFrom":sQuery(id+"F0.wireOp",EDGE,"E13.0.8.0")}),-1.0]])]});
            var Q12;
            Q12=makeQuery(id+"F0.imprint","IMPRINT",FACE,{"disambiguationData":[TD([[makeQuery(id+"F0.imprint","IMPRINT",EDGE,{"derivedFrom":sQuery(id+"F0.wireOp",EDGE,"E13.0.7.4")}),1.0]])]});
            var Q13;
            Q13=makeQuery(id+"F0.imprint","IMPRINT",FACE,{"disambiguationData":[TD([[makeQuery(id+"F0.imprint","IMPRINT",EDGE,{"derivedFrom":sQuery(id+"F0.wireOp",EDGE,"E13.0.7.8")}),1.0]])]});
            var Q14;
            Q14=makeQuery(id+"F0.imprint","IMPRINT",FACE,{"disambiguationData":[TD([[makeQuery(id+"F0.imprint","IMPRINT",EDGE,{"derivedFrom":sQuery(id+"F0.wireOp",EDGE,"E13.0.7.0")}),-1.0]])]});
            var Q15;
            Q15=makeQuery(id+"F0.imprint","IMPRINT",FACE,{"disambiguationData":[TD([[makeQuery(id+"F0.imprint","IMPRINT",EDGE,{"derivedFrom":sQuery(id+"F0.wireOp",EDGE,"E13.0.6.0")}),-1.0]])]});
            var Q16;
            Q16=makeQuery(id+"F0.imprint","IMPRINT",FACE,{"disambiguationData":[TD([[makeQuery(id+"F0.imprint","IMPRINT",EDGE,{"derivedFrom":sQuery(id+"F0.wireOp",EDGE,"E13.0.6.8")}),1.0]])]});
            var Q17;
            Q17=makeQuery(id+"F0.imprint","IMPRINT",FACE,{"disambiguationData":[TD([[makeQuery(id+"F0.imprint","IMPRINT",EDGE,{"derivedFrom":sQuery(id+"F0.wireOp",EDGE,"E13.0.6.4")}),1.0]])]});
            var Q18;
            Q18=makeQuery(id+"F0.imprint","IMPRINT",FACE,{"disambiguationData":[TD([[makeQuery(id+"F0.imprint","IMPRINT",EDGE,{"derivedFrom":sQuery(id+"F0.wireOp",EDGE,"E13.0.5.4")}),1.0]])]});
            var Q19;
            Q19=makeQuery(id+"F0.imprint","IMPRINT",FACE,{"disambiguationData":[TD([[makeQuery(id+"F0.imprint","IMPRINT",EDGE,{"derivedFrom":sQuery(id+"F0.wireOp",EDGE,"E13.0.5.8")}),1.0]])]});
            var Q20;
            Q20=makeQuery(id+"F0.imprint","IMPRINT",FACE,{"disambiguationData":[TD([[makeQuery(id+"F0.imprint","IMPRINT",EDGE,{"derivedFrom":sQuery(id+"F0.wireOp",EDGE,"E13.0.5.0")}),-1.0]])]});
            var Q21;
            Q21=makeQuery(id+"F0.imprint","IMPRINT",FACE,{"disambiguationData":[TD([[makeQuery(id+"F0.imprint","IMPRINT",EDGE,{"derivedFrom":sQuery(id+"F0.wireOp",EDGE,"E13.0.4.8")}),1.0]])]});
            var Q22;
            Q22=makeQuery(id+"F0.imprint","IMPRINT",FACE,{"disambiguationData":[TD([[makeQuery(id+"F0.imprint","IMPRINT",EDGE,{"derivedFrom":sQuery(id+"F0.wireOp",EDGE,"E13.0.4.4")}),1.0]])]});
            var Q23;
            Q23=makeQuery(id+"F0.imprint","IMPRINT",FACE,{"disambiguationData":[TD([[makeQuery(id+"F0.imprint","IMPRINT",EDGE,{"derivedFrom":sQuery(id+"F0.wireOp",EDGE,"E13.0.4.0")}),-1.0]])]});
            var Q24;
            Q24=makeQuery(id+"F0.imprint","IMPRINT",FACE,{"disambiguationData":[TD([[makeQuery(id+"F0.imprint","IMPRINT",EDGE,{"derivedFrom":sQuery(id+"F0.wireOp",EDGE,"E13.0.3.4")}),1.0]])]});
            var Q25;
            Q25=makeQuery(id+"F0.imprint","IMPRINT",FACE,{"disambiguationData":[TD([[makeQuery(id+"F0.imprint","IMPRINT",EDGE,{"derivedFrom":sQuery(id+"F0.wireOp",EDGE,"E13.0.3.8")}),1.0]])]});
            var Q26;
            Q26=makeQuery(id+"F0.imprint","IMPRINT",FACE,{"disambiguationData":[TD([[makeQuery(id+"F0.imprint","IMPRINT",EDGE,{"derivedFrom":sQuery(id+"F0.wireOp",EDGE,"E13.0.3.0")}),-1.0]])]});
            var Q27;
            Q27=makeQuery(id+"F0.imprint","IMPRINT",FACE,{"disambiguationData":[TD([[makeQuery(id+"F0.imprint","IMPRINT",EDGE,{"derivedFrom":sQuery(id+"F0.wireOp",EDGE,"E13.0.2.8")}),1.0]])]});
            var Q28;
            Q28=makeQuery(id+"F0.imprint","IMPRINT",FACE,{"disambiguationData":[TD([[makeQuery(id+"F0.imprint","IMPRINT",EDGE,{"derivedFrom":sQuery(id+"F0.wireOp",EDGE,"E13.0.2.4")}),1.0]])]});
            var Q29;
            Q29=makeQuery(id+"F0.imprint","IMPRINT",FACE,{"disambiguationData":[TD([[makeQuery(id+"F0.imprint","IMPRINT",EDGE,{"derivedFrom":sQuery(id+"F0.wireOp",EDGE,"E13.0.2.0")}),-1.0]])]});
            var Q30;
            Q30=makeQuery(id+"F0.imprint","IMPRINT",FACE,{"disambiguationData":[TD([[makeQuery(id+"F0.imprint","IMPRINT",EDGE,{"derivedFrom":sQuery(id+"F0.wireOp",EDGE,"E13.0.1.8")}),1.0]])]});
            var Q31;
            Q31=makeQuery(id+"F0.imprint","IMPRINT",FACE,{"disambiguationData":[TD([[makeQuery(id+"F0.imprint","IMPRINT",EDGE,{"derivedFrom":sQuery(id+"F0.wireOp",EDGE,"E13.0.1.4")}),1.0]])]});
            var Q32;
            Q32=makeQuery(id+"F0.imprint","IMPRINT",FACE,{"disambiguationData":[TD([[makeQuery(id+"F0.imprint","IMPRINT",EDGE,{"derivedFrom":sQuery(id+"F0.wireOp",EDGE,"E13.0.1.0")}),-1.0]])]});
            var Q33;
            {var subQ3=sQuery(id+"F0.wireOp",EDGE,"E1.bottom");Q33=makeQuery(id+"F0.imprint","IMPRINT",FACE,{"disambiguationData":[TD([[makeQuery(id+"F0.imprint","IMPRINT",EDGE,{"derivedFrom":subQ3}),1.0]])]});}
            var Q34;
            Q34=makeQuery(id+"F0.imprint","IMPRINT",FACE,{"disambiguationData":[TD([[makeQuery(id+"F0.imprint","IMPRINT",EDGE,{"derivedFrom":sQuery(id+"F0.wireOp",EDGE,"E9.MirrorCS")}),1.0]])]});
            var Q35;
            Q35=makeQuery(id+"F0.imprint","IMPRINT",FACE,{"disambiguationData":[TD([[makeQuery(id+"F0.imprint","IMPRINT",EDGE,{"derivedFrom":sQuery(id+"F0.wireOp",EDGE,"E4")}),1.0]])]});
            var Q36;
            Q36=makeQuery(id+"F0.imprint","IMPRINT",FACE,{"disambiguationData":[TD([[makeQuery(id+"F0.imprint","IMPRINT",EDGE,{"derivedFrom":sQuery(id+"F0.wireOp",EDGE,"E2")}),-1.0]])]});
            var Q37;
            Q37=makeQuery(id+"F0.imprint","IMPRINT",FACE,{"disambiguationData":[TD([[makeQuery(id+"F0.imprint","IMPRINT",EDGE,{"derivedFrom":sQuery(id+"F0.wireOp",EDGE,"E14.0.1.0")}),1.0]])]});
            var Q38;
            Q38=makeQuery(id+"F0.imprint","IMPRINT",FACE,{"disambiguationData":[TD([[makeQuery(id+"F0.imprint","IMPRINT",EDGE,{"derivedFrom":sQuery(id+"F0.wireOp",EDGE,"E14.0.1.4")}),1.0]])]});
            var Q39;
            Q39=makeQuery(id+"F0.imprint","IMPRINT",FACE,{"disambiguationData":[TD([[makeQuery(id+"F0.imprint","IMPRINT",EDGE,{"derivedFrom":sQuery(id+"F0.wireOp",EDGE,"E14.0.1.8")}),1.0]])]});
            var Q40;
            Q40=makeQuery(id+"F0.imprint","IMPRINT",FACE,{"disambiguationData":[TD([[makeQuery(id+"F0.imprint","IMPRINT",EDGE,{"derivedFrom":sQuery(id+"F0.wireOp",EDGE,"E14.0.2.8")}),1.0]])]});
            var Q41;
            Q41=makeQuery(id+"F0.imprint","IMPRINT",FACE,{"disambiguationData":[TD([[makeQuery(id+"F0.imprint","IMPRINT",EDGE,{"derivedFrom":sQuery(id+"F0.wireOp",EDGE,"E14.0.2.4")}),1.0]])]});
            var Q42;
            Q42=makeQuery(id+"F0.imprint","IMPRINT",FACE,{"disambiguationData":[TD([[makeQuery(id+"F0.imprint","IMPRINT",EDGE,{"derivedFrom":sQuery(id+"F0.wireOp",EDGE,"E14.0.2.0")}),1.0]])]});
            var Q43;
            Q43=makeQuery(id+"F0.imprint","IMPRINT",FACE,{"disambiguationData":[TD([[makeQuery(id+"F0.imprint","IMPRINT",EDGE,{"derivedFrom":sQuery(id+"F0.wireOp",EDGE,"E14.0.3.4")}),1.0]])]});
            var Q44;
            Q44=makeQuery(id+"F0.imprint","IMPRINT",FACE,{"disambiguationData":[TD([[makeQuery(id+"F0.imprint","IMPRINT",EDGE,{"derivedFrom":sQuery(id+"F0.wireOp",EDGE,"E14.0.3.0")}),1.0]])]});
            var Q45;
            Q45=makeQuery(id+"F0.imprint","IMPRINT",FACE,{"disambiguationData":[TD([[makeQuery(id+"F0.imprint","IMPRINT",EDGE,{"derivedFrom":sQuery(id+"F0.wireOp",EDGE,"E14.0.3.8")}),1.0]])]});
            var Q46;
            Q46=makeQuery(id+"F0.imprint","IMPRINT",FACE,{"disambiguationData":[TD([[makeQuery(id+"F0.imprint","IMPRINT",EDGE,{"derivedFrom":sQuery(id+"F0.wireOp",EDGE,"E14.0.4.8")}),1.0]])]});
            var Q47;
            Q47=makeQuery(id+"F0.imprint","IMPRINT",FACE,{"disambiguationData":[TD([[makeQuery(id+"F0.imprint","IMPRINT",EDGE,{"derivedFrom":sQuery(id+"F0.wireOp",EDGE,"E14.0.4.4")}),1.0]])]});
            var Q48;
            Q48=makeQuery(id+"F0.imprint","IMPRINT",FACE,{"disambiguationData":[TD([[makeQuery(id+"F0.imprint","IMPRINT",EDGE,{"derivedFrom":sQuery(id+"F0.wireOp",EDGE,"E14.0.4.0")}),1.0]])]});
            var Q49;
            Q49=makeQuery(id+"F0.imprint","IMPRINT",FACE,{"disambiguationData":[TD([[makeQuery(id+"F0.imprint","IMPRINT",EDGE,{"derivedFrom":sQuery(id+"F0.wireOp",EDGE,"E14.0.5.0")}),1.0]])]});
            var Q50;
            Q50=makeQuery(id+"F0.imprint","IMPRINT",FACE,{"disambiguationData":[TD([[makeQuery(id+"F0.imprint","IMPRINT",EDGE,{"derivedFrom":sQuery(id+"F0.wireOp",EDGE,"E14.0.5.4")}),1.0]])]});
            var Q51;
            Q51=makeQuery(id+"F0.imprint","IMPRINT",FACE,{"disambiguationData":[TD([[makeQuery(id+"F0.imprint","IMPRINT",EDGE,{"derivedFrom":sQuery(id+"F0.wireOp",EDGE,"E14.0.5.8")}),1.0]])]});
            var Q52;
            Q52=makeQuery(id+"F0.imprint","IMPRINT",FACE,{"disambiguationData":[TD([[makeQuery(id+"F0.imprint","IMPRINT",EDGE,{"derivedFrom":sQuery(id+"F0.wireOp",EDGE,"E14.0.6.0")}),1.0]])]});
            var Q53;
            Q53=makeQuery(id+"F0.imprint","IMPRINT",FACE,{"disambiguationData":[TD([[makeQuery(id+"F0.imprint","IMPRINT",EDGE,{"derivedFrom":sQuery(id+"F0.wireOp",EDGE,"E14.0.6.4")}),1.0]])]});
            var Q54;
            Q54=makeQuery(id+"F0.imprint","IMPRINT",FACE,{"disambiguationData":[TD([[makeQuery(id+"F0.imprint","IMPRINT",EDGE,{"derivedFrom":sQuery(id+"F0.wireOp",EDGE,"E14.0.6.8")}),1.0]])]});
            var Q55;
            Q55=makeQuery(id+"F0.imprint","IMPRINT",FACE,{"disambiguationData":[TD([[makeQuery(id+"F0.imprint","IMPRINT",EDGE,{"derivedFrom":sQuery(id+"F0.wireOp",EDGE,"E14.0.7.8")}),1.0]])]});
            var Q56;
            Q56=makeQuery(id+"F0.imprint","IMPRINT",FACE,{"disambiguationData":[TD([[makeQuery(id+"F0.imprint","IMPRINT",EDGE,{"derivedFrom":sQuery(id+"F0.wireOp",EDGE,"E14.0.7.4")}),1.0]])]});
            var Q57;
            Q57=makeQuery(id+"F0.imprint","IMPRINT",FACE,{"disambiguationData":[TD([[makeQuery(id+"F0.imprint","IMPRINT",EDGE,{"derivedFrom":sQuery(id+"F0.wireOp",EDGE,"E14.0.7.0")}),1.0]])]});
            var Q58;
            Q58=makeQuery(id+"F0.imprint","IMPRINT",FACE,{"disambiguationData":[TD([[makeQuery(id+"F0.imprint","IMPRINT",EDGE,{"derivedFrom":sQuery(id+"F0.wireOp",EDGE,"E14.0.8.4")}),1.0]])]});
            var Q59;
            Q59=makeQuery(id+"F0.imprint","IMPRINT",FACE,{"disambiguationData":[TD([[makeQuery(id+"F0.imprint","IMPRINT",EDGE,{"derivedFrom":sQuery(id+"F0.wireOp",EDGE,"E14.0.8.0")}),1.0]])]});
            var Q60;
            Q60=makeQuery(id+"F0.imprint","IMPRINT",FACE,{"disambiguationData":[TD([[makeQuery(id+"F0.imprint","IMPRINT",EDGE,{"derivedFrom":sQuery(id+"F0.wireOp",EDGE,"E14.0.8.8")}),1.0]])]});
            var Q61;
            Q61=makeQuery(id+"F0.imprint","IMPRINT",FACE,{"disambiguationData":[TD([[makeQuery(id+"F0.imprint","IMPRINT",EDGE,{"derivedFrom":sQuery(id+"F0.wireOp",EDGE,"E14.0.9.4")}),1.0]])]});
            var Q62;
            Q62=makeQuery(id+"F0.imprint","IMPRINT",FACE,{"disambiguationData":[TD([[makeQuery(id+"F0.imprint","IMPRINT",EDGE,{"derivedFrom":sQuery(id+"F0.wireOp",EDGE,"E14.0.9.0")}),1.0]])]});
            var Q63;
            Q63=makeQuery(id+"F0.imprint","IMPRINT",FACE,{"disambiguationData":[TD([[makeQuery(id+"F0.imprint","IMPRINT",EDGE,{"derivedFrom":sQuery(id+"F0.wireOp",EDGE,"E14.0.9.8")}),1.0]])]});
            extrude(context, id + "F2", {"entities" : qUnion([Q0, Q1, Q2, Q3, Q4, Q5, Q6, Q7, Q8, Q9, Q10, Q11, Q12, Q13, Q14, Q15, Q16, Q17, Q18, Q19, Q20, Q21, Q22, Q23, Q24, Q25, Q26, Q27, Q28, Q29, Q30, Q31, Q32, Q33, Q34, Q35, Q36, Q37, Q38, Q39, Q40, Q41, Q42, Q43, Q44, Q45, Q46, Q47, Q48, Q49, Q50, Q51, Q52, Q53, Q54, Q55, Q56, Q57, Q58, Q59, Q60, Q61, Q62, Q63]), "operationType" : NewBodyOperationType.ADD, "depth" : 2 * mm, "offsetDistance" : 25 * mm});
        }
        {
            var Q0;
            Q0=makeQuery(id+"F2.opExtrude","CAP_EDGE",EDGE,{"disambiguationData":[OSD([sQuery(id+"F0.wireOp",EDGE,"E13.0.10.8")])],"isStart":false});
            var Q1;
            Q1=makeQuery(id+"F2.opExtrude","CAP_EDGE",EDGE,{"disambiguationData":[OSD([sQuery(id+"F0.wireOp",EDGE,"E13.0.10.9")])],"isStart":false});
            var Q2;
            Q2=makeQuery(id+"F2.opExtrude","CAP_EDGE",EDGE,{"disambiguationData":[OSD([sQuery(id+"F0.wireOp",EDGE,"E13.0.10.10")])],"isStart":false});
            var Q3;
            Q3=makeQuery(id+"F2.opExtrude","CAP_EDGE",EDGE,{"disambiguationData":[OSD([sQuery(id+"F0.wireOp",EDGE,"E13.0.10.11")])],"isStart":false});
            var Q4;
            Q4=makeQuery(id+"F2.opExtrude","CAP_EDGE",EDGE,{"disambiguationData":[OSD([sQuery(id+"F0.wireOp",EDGE,"E13.0.10.3")])],"isStart":false});
            var Q5;
            Q5=makeQuery(id+"F2.opExtrude","CAP_EDGE",EDGE,{"disambiguationData":[OSD([sQuery(id+"F0.wireOp",EDGE,"E13.0.10.0")])],"isStart":false});
            var Q6;
            Q6=makeQuery(id+"F2.opExtrude","CAP_EDGE",EDGE,{"disambiguationData":[OSD([sQuery(id+"F0.wireOp",EDGE,"E13.0.10.1"),sQuery(id+"F0.wireOp",EDGE,"E13.0.10.2")])],"isStart":false});
            var Q7;
            Q7=makeQuery(id+"F2.opExtrude","CAP_EDGE",EDGE,{"disambiguationData":[OSD([sQuery(id+"F0.wireOp",EDGE,"E13.0.10.5")])],"isStart":false});
            var Q8;
            Q8=makeQuery(id+"F2.opExtrude","CAP_EDGE",EDGE,{"disambiguationData":[OSD([sQuery(id+"F0.wireOp",EDGE,"E13.0.10.4"),sQuery(id+"F0.wireOp",EDGE,"E13.0.10.7")])],"isStart":false});
            var Q9;
            Q9=makeQuery(id+"F2.opExtrude","CAP_EDGE",EDGE,{"disambiguationData":[OSD([sQuery(id+"F0.wireOp",EDGE,"E13.0.10.6")])],"isStart":false});
            var Q10;
            Q10=makeQuery(id+"F2.opExtrude","CAP_FACE",FACE,{"disambiguationData":[OSD([sQuery(id+"F0.wireOp",EDGE,"E13.0.9.8"),sQuery(id+"F0.wireOp",EDGE,"E13.0.9.9"),sQuery(id+"F0.wireOp",EDGE,"E13.0.9.10"),sQuery(id+"F0.wireOp",EDGE,"E13.0.9.11")])],"isStart":false});
            var Q11;
            Q11=makeQuery(id+"F2.opExtrude","CAP_FACE",FACE,{"disambiguationData":[OSD([sQuery(id+"F0.wireOp",EDGE,"E13.0.9.4"),sQuery(id+"F0.wireOp",EDGE,"E13.0.9.5"),sQuery(id+"F0.wireOp",EDGE,"E13.0.9.6"),sQuery(id+"F0.wireOp",EDGE,"E13.0.9.7")])],"isStart":false});
            var Q12;
            Q12=makeQuery(id+"F2.opExtrude","CAP_FACE",FACE,{"disambiguationData":[OSD([sQuery(id+"F0.wireOp",EDGE,"E13.0.9.0"),sQuery(id+"F0.wireOp",EDGE,"E13.0.9.1"),sQuery(id+"F0.wireOp",EDGE,"E13.0.9.2"),sQuery(id+"F0.wireOp",EDGE,"E13.0.9.3")])],"isStart":false});
            var Q13;
            Q13=makeQuery(id+"F2.opExtrude","CAP_FACE",FACE,{"disambiguationData":[OSD([sQuery(id+"F0.wireOp",EDGE,"E13.0.8.0"),sQuery(id+"F0.wireOp",EDGE,"E13.0.8.1"),sQuery(id+"F0.wireOp",EDGE,"E13.0.8.2"),sQuery(id+"F0.wireOp",EDGE,"E13.0.8.3")])],"isStart":false});
            var Q14;
            Q14=makeQuery(id+"F2.opExtrude","CAP_FACE",FACE,{"disambiguationData":[OSD([sQuery(id+"F0.wireOp",EDGE,"E13.0.8.8"),sQuery(id+"F0.wireOp",EDGE,"E13.0.8.9"),sQuery(id+"F0.wireOp",EDGE,"E13.0.8.10"),sQuery(id+"F0.wireOp",EDGE,"E13.0.8.11")])],"isStart":false});
            var Q15;
            Q15=makeQuery(id+"F2.opExtrude","CAP_FACE",FACE,{"disambiguationData":[OSD([sQuery(id+"F0.wireOp",EDGE,"E13.0.8.4"),sQuery(id+"F0.wireOp",EDGE,"E13.0.8.5"),sQuery(id+"F0.wireOp",EDGE,"E13.0.8.6"),sQuery(id+"F0.wireOp",EDGE,"E13.0.8.7")])],"isStart":false});
            var Q16;
            Q16=makeQuery(id+"F2.opExtrude","CAP_FACE",FACE,{"disambiguationData":[OSD([sQuery(id+"F0.wireOp",EDGE,"E13.0.7.8"),sQuery(id+"F0.wireOp",EDGE,"E13.0.7.9"),sQuery(id+"F0.wireOp",EDGE,"E13.0.7.10"),sQuery(id+"F0.wireOp",EDGE,"E13.0.7.11")])],"isStart":false});
            var Q17;
            Q17=makeQuery(id+"F2.opExtrude","CAP_FACE",FACE,{"disambiguationData":[OSD([sQuery(id+"F0.wireOp",EDGE,"E13.0.6.8"),sQuery(id+"F0.wireOp",EDGE,"E13.0.6.9"),sQuery(id+"F0.wireOp",EDGE,"E13.0.6.10"),sQuery(id+"F0.wireOp",EDGE,"E13.0.6.11")])],"isStart":false});
            var Q18;
            Q18=makeQuery(id+"F2.opExtrude","CAP_FACE",FACE,{"disambiguationData":[OSD([sQuery(id+"F0.wireOp",EDGE,"E13.0.5.8"),sQuery(id+"F0.wireOp",EDGE,"E13.0.5.9"),sQuery(id+"F0.wireOp",EDGE,"E13.0.5.10"),sQuery(id+"F0.wireOp",EDGE,"E13.0.5.11")])],"isStart":false});
            var Q19;
            Q19=makeQuery(id+"F2.opExtrude","CAP_FACE",FACE,{"disambiguationData":[OSD([sQuery(id+"F0.wireOp",EDGE,"E13.0.4.8"),sQuery(id+"F0.wireOp",EDGE,"E13.0.4.9"),sQuery(id+"F0.wireOp",EDGE,"E13.0.4.10"),sQuery(id+"F0.wireOp",EDGE,"E13.0.4.11")])],"isStart":false});
            var Q20;
            Q20=makeQuery(id+"F2.opExtrude","CAP_FACE",FACE,{"disambiguationData":[OSD([sQuery(id+"F0.wireOp",EDGE,"E13.0.3.8"),sQuery(id+"F0.wireOp",EDGE,"E13.0.3.9"),sQuery(id+"F0.wireOp",EDGE,"E13.0.3.10"),sQuery(id+"F0.wireOp",EDGE,"E13.0.3.11")])],"isStart":false});
            var Q21;
            Q21=makeQuery(id+"F2.opExtrude","CAP_FACE",FACE,{"disambiguationData":[OSD([sQuery(id+"F0.wireOp",EDGE,"E13.0.2.8"),sQuery(id+"F0.wireOp",EDGE,"E13.0.2.9"),sQuery(id+"F0.wireOp",EDGE,"E13.0.2.10"),sQuery(id+"F0.wireOp",EDGE,"E13.0.2.11")])],"isStart":false});
            var Q22;
            Q22=makeQuery(id+"F2.opExtrude","CAP_FACE",FACE,{"disambiguationData":[OSD([sQuery(id+"F0.wireOp",EDGE,"E13.0.1.8"),sQuery(id+"F0.wireOp",EDGE,"E13.0.1.9"),sQuery(id+"F0.wireOp",EDGE,"E13.0.1.10"),sQuery(id+"F0.wireOp",EDGE,"E13.0.1.11")])],"isStart":false});
            var Q23;
            Q23=makeQuery(id+"F2.opExtrude","CAP_FACE",FACE,{"disambiguationData":[OSD([sQuery(id+"F0.wireOp",EDGE,"E1.bottom"),sQuery(id+"F0.wireOp",EDGE,"E1.top"),sQuery(id+"F0.wireOp",EDGE,"E1.left"),sQuery(id+"F0.wireOp",EDGE,"E1.right")])],"isStart":false});
            var Q24;
            Q24=makeQuery(id+"F2.opExtrude","CAP_FACE",FACE,{"disambiguationData":[OSD([sQuery(id+"F0.wireOp",EDGE,"E14.0.1.4"),sQuery(id+"F0.wireOp",EDGE,"E14.0.1.5"),sQuery(id+"F0.wireOp",EDGE,"E14.0.1.6"),sQuery(id+"F0.wireOp",EDGE,"E14.0.1.7")])],"isStart":false});
            var Q25;
            Q25=makeQuery(id+"F2.opExtrude","CAP_FACE",FACE,{"disambiguationData":[OSD([sQuery(id+"F0.wireOp",EDGE,"E14.0.2.4"),sQuery(id+"F0.wireOp",EDGE,"E14.0.2.5"),sQuery(id+"F0.wireOp",EDGE,"E14.0.2.6"),sQuery(id+"F0.wireOp",EDGE,"E14.0.2.7")])],"isStart":false});
            var Q26;
            Q26=makeQuery(id+"F2.opExtrude","CAP_FACE",FACE,{"disambiguationData":[OSD([sQuery(id+"F0.wireOp",EDGE,"E14.0.3.4"),sQuery(id+"F0.wireOp",EDGE,"E14.0.3.5"),sQuery(id+"F0.wireOp",EDGE,"E14.0.3.6"),sQuery(id+"F0.wireOp",EDGE,"E14.0.3.7")])],"isStart":false});
            var Q27;
            Q27=makeQuery(id+"F2.opExtrude","CAP_FACE",FACE,{"disambiguationData":[OSD([sQuery(id+"F0.wireOp",EDGE,"E14.0.4.4"),sQuery(id+"F0.wireOp",EDGE,"E14.0.4.5"),sQuery(id+"F0.wireOp",EDGE,"E14.0.4.6"),sQuery(id+"F0.wireOp",EDGE,"E14.0.4.7")])],"isStart":false});
            var Q28;
            Q28=makeQuery(id+"F2.opExtrude","CAP_FACE",FACE,{"disambiguationData":[OSD([sQuery(id+"F0.wireOp",EDGE,"E14.0.5.4"),sQuery(id+"F0.wireOp",EDGE,"E14.0.5.5"),sQuery(id+"F0.wireOp",EDGE,"E14.0.5.6"),sQuery(id+"F0.wireOp",EDGE,"E14.0.5.7")])],"isStart":false});
            var Q29;
            Q29=makeQuery(id+"F2.opExtrude","CAP_FACE",FACE,{"disambiguationData":[OSD([sQuery(id+"F0.wireOp",EDGE,"E14.0.6.4"),sQuery(id+"F0.wireOp",EDGE,"E14.0.6.5"),sQuery(id+"F0.wireOp",EDGE,"E14.0.6.6"),sQuery(id+"F0.wireOp",EDGE,"E14.0.6.7")])],"isStart":false});
            var Q30;
            Q30=makeQuery(id+"F2.opExtrude","CAP_FACE",FACE,{"disambiguationData":[OSD([sQuery(id+"F0.wireOp",EDGE,"E14.0.7.4"),sQuery(id+"F0.wireOp",EDGE,"E14.0.7.5"),sQuery(id+"F0.wireOp",EDGE,"E14.0.7.6"),sQuery(id+"F0.wireOp",EDGE,"E14.0.7.7")])],"isStart":false});
            var Q31;
            Q31=makeQuery(id+"F2.opExtrude","CAP_FACE",FACE,{"disambiguationData":[OSD([sQuery(id+"F0.wireOp",EDGE,"E14.0.8.4"),sQuery(id+"F0.wireOp",EDGE,"E14.0.8.5"),sQuery(id+"F0.wireOp",EDGE,"E14.0.8.6"),sQuery(id+"F0.wireOp",EDGE,"E14.0.8.7")])],"isStart":false});
            var Q32;
            Q32=makeQuery(id+"F2.opExtrude","CAP_FACE",FACE,{"disambiguationData":[OSD([sQuery(id+"F0.wireOp",EDGE,"E14.0.9.4"),sQuery(id+"F0.wireOp",EDGE,"E14.0.9.5"),sQuery(id+"F0.wireOp",EDGE,"E14.0.9.6"),sQuery(id+"F0.wireOp",EDGE,"E14.0.9.7")])],"isStart":false});
            var Q33;
            Q33=makeQuery(id+"F2.opExtrude","CAP_FACE",FACE,{"disambiguationData":[OSD([sQuery(id+"F0.wireOp",EDGE,"E14.0.9.8"),sQuery(id+"F0.wireOp",EDGE,"E14.0.9.9"),sQuery(id+"F0.wireOp",EDGE,"E14.0.9.10"),sQuery(id+"F0.wireOp",EDGE,"E14.0.9.11")])],"isStart":false});
            var Q34;
            Q34=makeQuery(id+"F2.opExtrude","CAP_FACE",FACE,{"disambiguationData":[OSD([sQuery(id+"F0.wireOp",EDGE,"E14.0.9.0"),sQuery(id+"F0.wireOp",EDGE,"E14.0.9.1"),sQuery(id+"F0.wireOp",EDGE,"E14.0.9.2"),sQuery(id+"F0.wireOp",EDGE,"E14.0.9.3")])],"isStart":false});
            var Q35;
            Q35=makeQuery(id+"F2.opExtrude","CAP_FACE",FACE,{"disambiguationData":[OSD([sQuery(id+"F0.wireOp",EDGE,"E14.0.8.0"),sQuery(id+"F0.wireOp",EDGE,"E14.0.8.1"),sQuery(id+"F0.wireOp",EDGE,"E14.0.8.2"),sQuery(id+"F0.wireOp",EDGE,"E14.0.8.3")])],"isStart":false});
            var Q36;
            Q36=makeQuery(id+"F2.opExtrude","CAP_FACE",FACE,{"disambiguationData":[OSD([sQuery(id+"F0.wireOp",EDGE,"E14.0.8.8"),sQuery(id+"F0.wireOp",EDGE,"E14.0.8.9"),sQuery(id+"F0.wireOp",EDGE,"E14.0.8.10"),sQuery(id+"F0.wireOp",EDGE,"E14.0.8.11")])],"isStart":false});
            var Q37;
            Q37=makeQuery(id+"F2.opExtrude","CAP_FACE",FACE,{"disambiguationData":[OSD([sQuery(id+"F0.wireOp",EDGE,"E14.0.7.8"),sQuery(id+"F0.wireOp",EDGE,"E14.0.7.9"),sQuery(id+"F0.wireOp",EDGE,"E14.0.7.10"),sQuery(id+"F0.wireOp",EDGE,"E14.0.7.11")])],"isStart":false});
            var Q38;
            Q38=makeQuery(id+"F2.opExtrude","CAP_FACE",FACE,{"disambiguationData":[OSD([sQuery(id+"F0.wireOp",EDGE,"E14.0.7.0"),sQuery(id+"F0.wireOp",EDGE,"E14.0.7.1"),sQuery(id+"F0.wireOp",EDGE,"E14.0.7.2"),sQuery(id+"F0.wireOp",EDGE,"E14.0.7.3")])],"isStart":false});
            var Q39;
            Q39=makeQuery(id+"F2.opExtrude","CAP_FACE",FACE,{"disambiguationData":[OSD([sQuery(id+"F0.wireOp",EDGE,"E14.0.6.0"),sQuery(id+"F0.wireOp",EDGE,"E14.0.6.1"),sQuery(id+"F0.wireOp",EDGE,"E14.0.6.2"),sQuery(id+"F0.wireOp",EDGE,"E14.0.6.3")])],"isStart":false});
            var Q40;
            Q40=makeQuery(id+"F2.opExtrude","CAP_FACE",FACE,{"disambiguationData":[OSD([sQuery(id+"F0.wireOp",EDGE,"E14.0.6.8"),sQuery(id+"F0.wireOp",EDGE,"E14.0.6.9"),sQuery(id+"F0.wireOp",EDGE,"E14.0.6.10"),sQuery(id+"F0.wireOp",EDGE,"E14.0.6.11")])],"isStart":false});
            var Q41;
            Q41=makeQuery(id+"F2.opExtrude","CAP_FACE",FACE,{"disambiguationData":[OSD([sQuery(id+"F0.wireOp",EDGE,"E14.0.5.8"),sQuery(id+"F0.wireOp",EDGE,"E14.0.5.9"),sQuery(id+"F0.wireOp",EDGE,"E14.0.5.10"),sQuery(id+"F0.wireOp",EDGE,"E14.0.5.11")])],"isStart":false});
            var Q42;
            Q42=makeQuery(id+"F2.opExtrude","CAP_FACE",FACE,{"disambiguationData":[OSD([sQuery(id+"F0.wireOp",EDGE,"E14.0.5.0"),sQuery(id+"F0.wireOp",EDGE,"E14.0.5.1"),sQuery(id+"F0.wireOp",EDGE,"E14.0.5.2"),sQuery(id+"F0.wireOp",EDGE,"E14.0.5.3")])],"isStart":false});
            var Q43;
            Q43=makeQuery(id+"F2.opExtrude","CAP_FACE",FACE,{"disambiguationData":[OSD([sQuery(id+"F0.wireOp",EDGE,"E14.0.4.8"),sQuery(id+"F0.wireOp",EDGE,"E14.0.4.9"),sQuery(id+"F0.wireOp",EDGE,"E14.0.4.10"),sQuery(id+"F0.wireOp",EDGE,"E14.0.4.11")])],"isStart":false});
            var Q44;
            Q44=makeQuery(id+"F2.opExtrude","CAP_FACE",FACE,{"disambiguationData":[OSD([sQuery(id+"F0.wireOp",EDGE,"E14.0.4.0"),sQuery(id+"F0.wireOp",EDGE,"E14.0.4.1"),sQuery(id+"F0.wireOp",EDGE,"E14.0.4.2"),sQuery(id+"F0.wireOp",EDGE,"E14.0.4.3")])],"isStart":false});
            var Q45;
            Q45=makeQuery(id+"F2.opExtrude","CAP_FACE",FACE,{"disambiguationData":[OSD([sQuery(id+"F0.wireOp",EDGE,"E14.0.3.0"),sQuery(id+"F0.wireOp",EDGE,"E14.0.3.1"),sQuery(id+"F0.wireOp",EDGE,"E14.0.3.2"),sQuery(id+"F0.wireOp",EDGE,"E14.0.3.3")])],"isStart":false});
            var Q46;
            Q46=makeQuery(id+"F2.opExtrude","CAP_FACE",FACE,{"disambiguationData":[OSD([sQuery(id+"F0.wireOp",EDGE,"E14.0.3.8"),sQuery(id+"F0.wireOp",EDGE,"E14.0.3.9"),sQuery(id+"F0.wireOp",EDGE,"E14.0.3.10"),sQuery(id+"F0.wireOp",EDGE,"E14.0.3.11")])],"isStart":false});
            var Q47;
            Q47=makeQuery(id+"F2.opExtrude","CAP_FACE",FACE,{"disambiguationData":[OSD([sQuery(id+"F0.wireOp",EDGE,"E14.0.2.8"),sQuery(id+"F0.wireOp",EDGE,"E14.0.2.9"),sQuery(id+"F0.wireOp",EDGE,"E14.0.2.10"),sQuery(id+"F0.wireOp",EDGE,"E14.0.2.11")])],"isStart":false});
            var Q48;
            Q48=makeQuery(id+"F2.opExtrude","CAP_FACE",FACE,{"disambiguationData":[OSD([sQuery(id+"F0.wireOp",EDGE,"E14.0.2.0"),sQuery(id+"F0.wireOp",EDGE,"E14.0.2.1"),sQuery(id+"F0.wireOp",EDGE,"E14.0.2.2"),sQuery(id+"F0.wireOp",EDGE,"E14.0.2.3")])],"isStart":false});
            var Q49;
            Q49=makeQuery(id+"F2.opExtrude","CAP_FACE",FACE,{"disambiguationData":[OSD([sQuery(id+"F0.wireOp",EDGE,"E14.0.1.0"),sQuery(id+"F0.wireOp",EDGE,"E14.0.1.1"),sQuery(id+"F0.wireOp",EDGE,"E14.0.1.2"),sQuery(id+"F0.wireOp",EDGE,"E14.0.1.3")])],"isStart":false});
            var Q50;
            Q50=makeQuery(id+"F2.opExtrude","CAP_FACE",FACE,{"disambiguationData":[OSD([sQuery(id+"F0.wireOp",EDGE,"E14.0.1.8"),sQuery(id+"F0.wireOp",EDGE,"E14.0.1.9"),sQuery(id+"F0.wireOp",EDGE,"E14.0.1.10"),sQuery(id+"F0.wireOp",EDGE,"E14.0.1.11")])],"isStart":false});
            var Q51;
            Q51=makeQuery(id+"F2.opExtrude","CAP_FACE",FACE,{"disambiguationData":[OSD([sQuery(id+"F0.wireOp",EDGE,"E2"),sQuery(id+"F0.wireOp",EDGE,"E3"),sQuery(id+"F0.wireOp",EDGE,"E5"),sQuery(id+"F0.wireOp",EDGE,"E6")])],"isStart":false});
            var Q52;
            Q52=makeQuery(id+"F2.opExtrude","CAP_FACE",FACE,{"disambiguationData":[OSD([sQuery(id+"F0.wireOp",EDGE,"E9.MirrorCS"),sQuery(id+"F0.wireOp",EDGE,"E10.MirrorCS"),sQuery(id+"F0.wireOp",EDGE,"E11.MirrorCS"),sQuery(id+"F0.wireOp",EDGE,"E12.MirrorCS")])],"isStart":false});
            var Q53;
            Q53=makeQuery(id+"F2.opExtrude","CAP_FACE",FACE,{"disambiguationData":[OSD([sQuery(id+"F0.wireOp",EDGE,"E13.0.1.4"),sQuery(id+"F0.wireOp",EDGE,"E13.0.1.5"),sQuery(id+"F0.wireOp",EDGE,"E13.0.1.6"),sQuery(id+"F0.wireOp",EDGE,"E13.0.1.7")])],"isStart":false});
            var Q54;
            Q54=makeQuery(id+"F2.opExtrude","CAP_FACE",FACE,{"disambiguationData":[OSD([sQuery(id+"F0.wireOp",EDGE,"E13.0.1.0"),sQuery(id+"F0.wireOp",EDGE,"E13.0.1.1"),sQuery(id+"F0.wireOp",EDGE,"E13.0.1.2"),sQuery(id+"F0.wireOp",EDGE,"E13.0.1.3")])],"isStart":false});
            var Q55;
            Q55=makeQuery(id+"F2.opExtrude","CAP_FACE",FACE,{"disambiguationData":[OSD([sQuery(id+"F0.wireOp",EDGE,"E13.0.2.0"),sQuery(id+"F0.wireOp",EDGE,"E13.0.2.1"),sQuery(id+"F0.wireOp",EDGE,"E13.0.2.2"),sQuery(id+"F0.wireOp",EDGE,"E13.0.2.3")])],"isStart":false});
            var Q56;
            Q56=makeQuery(id+"F2.opExtrude","CAP_FACE",FACE,{"disambiguationData":[OSD([sQuery(id+"F0.wireOp",EDGE,"E13.0.2.4"),sQuery(id+"F0.wireOp",EDGE,"E13.0.2.5"),sQuery(id+"F0.wireOp",EDGE,"E13.0.2.6"),sQuery(id+"F0.wireOp",EDGE,"E13.0.2.7")])],"isStart":false});
            var Q57;
            Q57=makeQuery(id+"F2.opExtrude","CAP_FACE",FACE,{"disambiguationData":[OSD([sQuery(id+"F0.wireOp",EDGE,"E13.0.3.4"),sQuery(id+"F0.wireOp",EDGE,"E13.0.3.5"),sQuery(id+"F0.wireOp",EDGE,"E13.0.3.6"),sQuery(id+"F0.wireOp",EDGE,"E13.0.3.7")])],"isStart":false});
            var Q58;
            Q58=makeQuery(id+"F2.opExtrude","CAP_FACE",FACE,{"disambiguationData":[OSD([sQuery(id+"F0.wireOp",EDGE,"E13.0.4.4"),sQuery(id+"F0.wireOp",EDGE,"E13.0.4.5"),sQuery(id+"F0.wireOp",EDGE,"E13.0.4.6"),sQuery(id+"F0.wireOp",EDGE,"E13.0.4.7")])],"isStart":false});
            var Q59;
            Q59=makeQuery(id+"F2.opExtrude","CAP_FACE",FACE,{"disambiguationData":[OSD([sQuery(id+"F0.wireOp",EDGE,"E13.0.4.0"),sQuery(id+"F0.wireOp",EDGE,"E13.0.4.1"),sQuery(id+"F0.wireOp",EDGE,"E13.0.4.2"),sQuery(id+"F0.wireOp",EDGE,"E13.0.4.3")])],"isStart":false});
            var Q60;
            Q60=makeQuery(id+"F2.opExtrude","CAP_FACE",FACE,{"disambiguationData":[OSD([sQuery(id+"F0.wireOp",EDGE,"E13.0.3.0"),sQuery(id+"F0.wireOp",EDGE,"E13.0.3.1"),sQuery(id+"F0.wireOp",EDGE,"E13.0.3.2"),sQuery(id+"F0.wireOp",EDGE,"E13.0.3.3")])],"isStart":false});
            var Q61;
            Q61=makeQuery(id+"F2.opExtrude","CAP_FACE",FACE,{"disambiguationData":[OSD([sQuery(id+"F0.wireOp",EDGE,"E13.0.5.0"),sQuery(id+"F0.wireOp",EDGE,"E13.0.5.1"),sQuery(id+"F0.wireOp",EDGE,"E13.0.5.2"),sQuery(id+"F0.wireOp",EDGE,"E13.0.5.3")])],"isStart":false});
            var Q62;
            Q62=makeQuery(id+"F2.opExtrude","CAP_FACE",FACE,{"disambiguationData":[OSD([sQuery(id+"F0.wireOp",EDGE,"E13.0.5.4"),sQuery(id+"F0.wireOp",EDGE,"E13.0.5.5"),sQuery(id+"F0.wireOp",EDGE,"E13.0.5.6"),sQuery(id+"F0.wireOp",EDGE,"E13.0.5.7")])],"isStart":false});
            var Q63;
            Q63=makeQuery(id+"F2.opExtrude","CAP_FACE",FACE,{"disambiguationData":[OSD([sQuery(id+"F0.wireOp",EDGE,"E13.0.6.4"),sQuery(id+"F0.wireOp",EDGE,"E13.0.6.5"),sQuery(id+"F0.wireOp",EDGE,"E13.0.6.6"),sQuery(id+"F0.wireOp",EDGE,"E13.0.6.7")])],"isStart":false});
            var Q64;
            Q64=makeQuery(id+"F2.opExtrude","CAP_FACE",FACE,{"disambiguationData":[OSD([sQuery(id+"F0.wireOp",EDGE,"E13.0.7.4"),sQuery(id+"F0.wireOp",EDGE,"E13.0.7.5"),sQuery(id+"F0.wireOp",EDGE,"E13.0.7.6"),sQuery(id+"F0.wireOp",EDGE,"E13.0.7.7")])],"isStart":false});
            var Q65;
            Q65=makeQuery(id+"F2.opExtrude","CAP_FACE",FACE,{"disambiguationData":[OSD([sQuery(id+"F0.wireOp",EDGE,"E13.0.7.0"),sQuery(id+"F0.wireOp",EDGE,"E13.0.7.1"),sQuery(id+"F0.wireOp",EDGE,"E13.0.7.2"),sQuery(id+"F0.wireOp",EDGE,"E13.0.7.3")])],"isStart":false});
            var Q66;
            Q66=makeQuery(id+"F2.opExtrude","CAP_FACE",FACE,{"disambiguationData":[OSD([sQuery(id+"F0.wireOp",EDGE,"E13.0.6.0"),sQuery(id+"F0.wireOp",EDGE,"E13.0.6.1"),sQuery(id+"F0.wireOp",EDGE,"E13.0.6.2"),sQuery(id+"F0.wireOp",EDGE,"E13.0.6.3")])],"isStart":false});
            chamfer(context, id + "F3", {"entities" : qUnion([Q0, Q1, Q2, Q3, Q4, Q5, Q6, Q7, Q8, Q9, Q10, Q11, Q12, Q13, Q14, Q15, Q16, Q17, Q18, Q19, Q20, Q21, Q22, Q23, Q24, Q25, Q26, Q27, Q28, Q29, Q30, Q31, Q32, Q33, Q34, Q35, Q36, Q37, Q38, Q39, Q40, Q41, Q42, Q43, Q44, Q45, Q46, Q47, Q48, Q49, Q50, Q51, Q52, Q53, Q54, Q55, Q56, Q57, Q58, Q59, Q60, Q61, Q62, Q63, Q64, Q65, Q66]), "width" : 0.4 * mm, "tangentPropagation" : true});
        }
        {
            var Q0;
            {var subQ22=sQuery(id+"F0.wireOp",EDGE,"E0.right");Q0=makeQuery(id+"F0.imprint","IMPRINT",FACE,{"disambiguationData":[TD([[makeQuery(id+"F0.imprint","IMPRINT",EDGE,{"derivedFrom":subQ22}),1.0]])]});}
            var sketch = newSketch(context, id + "F4", { "sketchPlane" : qUnion([Q0])});
            skLineSegment(sketch, "E15.bottom", {"start": v(-4, 60.75) * mm, "end": v(4, 60.75) * mm});
            skLineSegment(sketch, "E15.top", {"start": v(-4, 62.75) * mm, "end": v(4, 62.75) * mm});
            skLineSegment(sketch, "E15.left", {"start": v(-4, 60.75) * mm, "end": v(-4, 62.75) * mm});
            skLineSegment(sketch, "E15.right", {"start": v(4, 60.75) * mm, "end": v(4, 62.75) * mm});
            skPoint(sketch, "E15.middle", {"position": v(0, 61.75) * mm});
            skLineSegment(sketch, "E16.0.1.0", {"start": v(-4, 54.25) * mm, "end": v(-4, 56.25) * mm});
            skLineSegment(sketch, "E16.0.1.1", {"start": v(-4, 54.25) * mm, "end": v(4, 54.25) * mm});
            skLineSegment(sketch, "E16.0.1.2", {"start": v(-4, 56.25) * mm, "end": v(4, 56.25) * mm});
            skLineSegment(sketch, "E16.0.1.3", {"start": v(4, 54.25) * mm, "end": v(4, 56.25) * mm});
            skLineSegment(sketch, "E16.0.2.0", {"start": v(-4, 47.75) * mm, "end": v(-4, 49.75) * mm});
            skLineSegment(sketch, "E16.0.2.1", {"start": v(-4, 47.75) * mm, "end": v(4, 47.75) * mm});
            skLineSegment(sketch, "E16.0.2.2", {"start": v(-4, 49.75) * mm, "end": v(4, 49.75) * mm});
            skLineSegment(sketch, "E16.0.2.3", {"start": v(4, 47.75) * mm, "end": v(4, 49.75) * mm});
            skLineSegment(sketch, "E16.0.3.0", {"start": v(-4, 41.25) * mm, "end": v(-4, 43.25) * mm});
            skLineSegment(sketch, "E16.0.3.1", {"start": v(-4, 41.25) * mm, "end": v(4, 41.25) * mm});
            skLineSegment(sketch, "E16.0.3.2", {"start": v(-4, 43.25) * mm, "end": v(4, 43.25) * mm});
            skLineSegment(sketch, "E16.0.3.3", {"start": v(4, 41.25) * mm, "end": v(4, 43.25) * mm});
            skLineSegment(sketch, "E16.0.4.0", {"start": v(-4, 34.75) * mm, "end": v(-4, 36.75) * mm});
            skLineSegment(sketch, "E16.0.4.1", {"start": v(-4, 34.75) * mm, "end": v(4, 34.75) * mm});
            skLineSegment(sketch, "E16.0.4.2", {"start": v(-4, 36.75) * mm, "end": v(4, 36.75) * mm});
            skLineSegment(sketch, "E16.0.4.3", {"start": v(4, 34.75) * mm, "end": v(4, 36.75) * mm});
            skLineSegment(sketch, "E16.0.5.0", {"start": v(-4, 28.25) * mm, "end": v(-4, 30.25) * mm});
            skLineSegment(sketch, "E16.0.5.1", {"start": v(-4, 28.25) * mm, "end": v(4, 28.25) * mm});
            skLineSegment(sketch, "E16.0.5.2", {"start": v(-4, 30.25) * mm, "end": v(4, 30.25) * mm});
            skLineSegment(sketch, "E16.0.5.3", {"start": v(4, 28.25) * mm, "end": v(4, 30.25) * mm});
            skLineSegment(sketch, "E16.0.6.0", {"start": v(-4, 21.75) * mm, "end": v(-4, 23.75) * mm});
            skLineSegment(sketch, "E16.0.6.1", {"start": v(-4, 21.75) * mm, "end": v(4, 21.75) * mm});
            skLineSegment(sketch, "E16.0.6.2", {"start": v(-4, 23.75) * mm, "end": v(4, 23.75) * mm});
            skLineSegment(sketch, "E16.0.6.3", {"start": v(4, 21.75) * mm, "end": v(4, 23.75) * mm});
            skLineSegment(sketch, "E16.0.7.0", {"start": v(-4, 15.25) * mm, "end": v(-4, 17.25) * mm});
            skLineSegment(sketch, "E16.0.7.1", {"start": v(-4, 15.25) * mm, "end": v(4, 15.25) * mm});
            skLineSegment(sketch, "E16.0.7.2", {"start": v(-4, 17.25) * mm, "end": v(4, 17.25) * mm});
            skLineSegment(sketch, "E16.0.7.3", {"start": v(4, 15.25) * mm, "end": v(4, 17.25) * mm});
            skLineSegment(sketch, "E16.0.8.0", {"start": v(-4, 8.75) * mm, "end": v(-4, 10.75) * mm});
            skLineSegment(sketch, "E16.0.8.1", {"start": v(-4, 8.75) * mm, "end": v(4, 8.75) * mm});
            skLineSegment(sketch, "E16.0.8.2", {"start": v(-4, 10.75) * mm, "end": v(4, 10.75) * mm});
            skLineSegment(sketch, "E16.0.8.3", {"start": v(4, 8.75) * mm, "end": v(4, 10.75) * mm});
            skLineSegment(sketch, "E16.0.9.0", {"start": v(-4, 2.25) * mm, "end": v(-4, 4.25) * mm});
            skLineSegment(sketch, "E16.0.9.1", {"start": v(-4, 2.25) * mm, "end": v(4, 2.25) * mm});
            skLineSegment(sketch, "E16.0.9.2", {"start": v(-4, 4.25) * mm, "end": v(4, 4.25) * mm});
            skLineSegment(sketch, "E16.0.9.3", {"start": v(4, 2.25) * mm, "end": v(4, 4.25) * mm});
            skLineSegment(sketch, "E16.0.10.0", {"start": v(-4, -4.25) * mm, "end": v(-4, -2.25) * mm});
            skLineSegment(sketch, "E16.0.10.1", {"start": v(-4, -4.25) * mm, "end": v(4, -4.25) * mm});
            skLineSegment(sketch, "E16.0.10.2", {"start": v(-4, -2.25) * mm, "end": v(4, -2.25) * mm});
            skLineSegment(sketch, "E16.0.10.3", {"start": v(4, -4.25) * mm, "end": v(4, -2.25) * mm});
            skLineSegment(sketch, "E16.0.11.0", {"start": v(-4, -10.75) * mm, "end": v(-4, -8.75) * mm});
            skLineSegment(sketch, "E16.0.11.1", {"start": v(-4, -10.75) * mm, "end": v(4, -10.75) * mm});
            skLineSegment(sketch, "E16.0.11.2", {"start": v(-4, -8.75) * mm, "end": v(4, -8.75) * mm});
            skLineSegment(sketch, "E16.0.11.3", {"start": v(4, -10.75) * mm, "end": v(4, -8.75) * mm});
            skLineSegment(sketch, "E16.0.12.0", {"start": v(-4, -17.25) * mm, "end": v(-4, -15.25) * mm});
            skLineSegment(sketch, "E16.0.12.1", {"start": v(-4, -17.25) * mm, "end": v(4, -17.25) * mm});
            skLineSegment(sketch, "E16.0.12.2", {"start": v(-4, -15.25) * mm, "end": v(4, -15.25) * mm});
            skLineSegment(sketch, "E16.0.12.3", {"start": v(4, -17.25) * mm, "end": v(4, -15.25) * mm});
            skLineSegment(sketch, "E16.0.13.0", {"start": v(-4, -23.75) * mm, "end": v(-4, -21.75) * mm});
            skLineSegment(sketch, "E16.0.13.1", {"start": v(-4, -23.75) * mm, "end": v(4, -23.75) * mm});
            skLineSegment(sketch, "E16.0.13.2", {"start": v(-4, -21.75) * mm, "end": v(4, -21.75) * mm});
            skLineSegment(sketch, "E16.0.13.3", {"start": v(4, -23.75) * mm, "end": v(4, -21.75) * mm});
            skLineSegment(sketch, "E16.0.14.0", {"start": v(-4, -30.25) * mm, "end": v(-4, -28.25) * mm});
            skLineSegment(sketch, "E16.0.14.1", {"start": v(-4, -30.25) * mm, "end": v(4, -30.25) * mm});
            skLineSegment(sketch, "E16.0.14.2", {"start": v(-4, -28.25) * mm, "end": v(4, -28.25) * mm});
            skLineSegment(sketch, "E16.0.14.3", {"start": v(4, -30.25) * mm, "end": v(4, -28.25) * mm});
            skLineSegment(sketch, "E16.0.15.0", {"start": v(-4, -36.75) * mm, "end": v(-4, -34.75) * mm});
            skLineSegment(sketch, "E16.0.15.1", {"start": v(-4, -36.75) * mm, "end": v(4, -36.75) * mm});
            skLineSegment(sketch, "E16.0.15.2", {"start": v(-4, -34.75) * mm, "end": v(4, -34.75) * mm});
            skLineSegment(sketch, "E16.0.15.3", {"start": v(4, -36.75) * mm, "end": v(4, -34.75) * mm});
            skLineSegment(sketch, "E16.0.16.0", {"start": v(-4, -43.25) * mm, "end": v(-4, -41.25) * mm});
            skLineSegment(sketch, "E16.0.16.1", {"start": v(-4, -43.25) * mm, "end": v(4, -43.25) * mm});
            skLineSegment(sketch, "E16.0.16.2", {"start": v(-4, -41.25) * mm, "end": v(4, -41.25) * mm});
            skLineSegment(sketch, "E16.0.16.3", {"start": v(4, -43.25) * mm, "end": v(4, -41.25) * mm});
            skLineSegment(sketch, "E16.0.17.0", {"start": v(-4, -49.75) * mm, "end": v(-4, -47.75) * mm});
            skLineSegment(sketch, "E16.0.17.1", {"start": v(-4, -49.75) * mm, "end": v(4, -49.75) * mm});
            skLineSegment(sketch, "E16.0.17.2", {"start": v(-4, -47.75) * mm, "end": v(4, -47.75) * mm});
            skLineSegment(sketch, "E16.0.17.3", {"start": v(4, -49.75) * mm, "end": v(4, -47.75) * mm});
            skLineSegment(sketch, "E16.0.18.0", {"start": v(-4, -56.25) * mm, "end": v(-4, -54.25) * mm});
            skLineSegment(sketch, "E16.0.18.1", {"start": v(-4, -56.25) * mm, "end": v(4, -56.25) * mm});
            skLineSegment(sketch, "E16.0.18.2", {"start": v(-4, -54.25) * mm, "end": v(4, -54.25) * mm});
            skLineSegment(sketch, "E16.0.18.3", {"start": v(4, -56.25) * mm, "end": v(4, -54.25) * mm});
            skLineSegment(sketch, "E16.0.19.0", {"start": v(-4, -62.75) * mm, "end": v(-4, -60.75) * mm});
            skLineSegment(sketch, "E16.0.19.1", {"start": v(-4, -62.75) * mm, "end": v(4, -62.75) * mm});
            skLineSegment(sketch, "E16.0.19.2", {"start": v(-4, -60.75) * mm, "end": v(4, -60.75) * mm});
            skLineSegment(sketch, "E16.0.19.3", {"start": v(4, -62.75) * mm, "end": v(4, -60.75) * mm});
            skLineSegment(sketch, "E16.direction1", {"start": v(-4, 60.75) * mm, "end": v(21, 60.75) * mm, "construction": true});
            skLineSegment(sketch, "E16.direction2", {"start": v(-4, 60.75) * mm, "end": v(-4, 54.25) * mm, "construction": true});
            skSolve(sketch);
        }
        {
            var Q0;
            Q0 = qSketchRegion(id + "F4", true);
            extrude(context, id + "F5", {"entities" : qUnion([Q0]), "operationType" : NewBodyOperationType.ADD, "oppositeDirection" : true, "depth" : 2 * mm, "offsetDistance" : 25 * mm});
        }
        {
            var Q0;
            Q0=makeQuery(id+"F5.opExtrude","CAP_FACE",FACE,{"disambiguationData":[OSD([sQuery(id+"F4.wireOp",EDGE,"E15.bottom"),sQuery(id+"F4.wireOp",EDGE,"E15.top"),sQuery(id+"F4.wireOp",EDGE,"E15.left"),sQuery(id+"F4.wireOp",EDGE,"E15.right")])],"isStart":false});
            var Q1;
            Q1=makeQuery(id+"F5.opExtrude","CAP_FACE",FACE,{"disambiguationData":[OSD([sQuery(id+"F4.wireOp",EDGE,"E16.0.1.0"),sQuery(id+"F4.wireOp",EDGE,"E16.0.1.1"),sQuery(id+"F4.wireOp",EDGE,"E16.0.1.2"),sQuery(id+"F4.wireOp",EDGE,"E16.0.1.3")])],"isStart":false});
            var Q2;
            Q2=makeQuery(id+"F5.opExtrude","CAP_FACE",FACE,{"disambiguationData":[OSD([sQuery(id+"F4.wireOp",EDGE,"E16.0.2.0"),sQuery(id+"F4.wireOp",EDGE,"E16.0.2.1"),sQuery(id+"F4.wireOp",EDGE,"E16.0.2.2"),sQuery(id+"F4.wireOp",EDGE,"E16.0.2.3")])],"isStart":false});
            var Q3;
            Q3=makeQuery(id+"F5.opExtrude","CAP_FACE",FACE,{"disambiguationData":[OSD([sQuery(id+"F4.wireOp",EDGE,"E16.0.3.0"),sQuery(id+"F4.wireOp",EDGE,"E16.0.3.1"),sQuery(id+"F4.wireOp",EDGE,"E16.0.3.2"),sQuery(id+"F4.wireOp",EDGE,"E16.0.3.3")])],"isStart":false});
            var Q4;
            Q4=makeQuery(id+"F5.opExtrude","CAP_FACE",FACE,{"disambiguationData":[OSD([sQuery(id+"F4.wireOp",EDGE,"E16.0.4.0"),sQuery(id+"F4.wireOp",EDGE,"E16.0.4.1"),sQuery(id+"F4.wireOp",EDGE,"E16.0.4.2"),sQuery(id+"F4.wireOp",EDGE,"E16.0.4.3")])],"isStart":false});
            var Q5;
            Q5=makeQuery(id+"F5.opExtrude","CAP_FACE",FACE,{"disambiguationData":[OSD([sQuery(id+"F4.wireOp",EDGE,"E16.0.5.0"),sQuery(id+"F4.wireOp",EDGE,"E16.0.5.1"),sQuery(id+"F4.wireOp",EDGE,"E16.0.5.2"),sQuery(id+"F4.wireOp",EDGE,"E16.0.5.3")])],"isStart":false});
            var Q6;
            Q6=makeQuery(id+"F5.opExtrude","CAP_FACE",FACE,{"disambiguationData":[OSD([sQuery(id+"F4.wireOp",EDGE,"E16.0.6.0"),sQuery(id+"F4.wireOp",EDGE,"E16.0.6.1"),sQuery(id+"F4.wireOp",EDGE,"E16.0.6.2"),sQuery(id+"F4.wireOp",EDGE,"E16.0.6.3")])],"isStart":false});
            var Q7;
            Q7=makeQuery(id+"F5.opExtrude","CAP_FACE",FACE,{"disambiguationData":[OSD([sQuery(id+"F4.wireOp",EDGE,"E16.0.7.0"),sQuery(id+"F4.wireOp",EDGE,"E16.0.7.1"),sQuery(id+"F4.wireOp",EDGE,"E16.0.7.2"),sQuery(id+"F4.wireOp",EDGE,"E16.0.7.3")])],"isStart":false});
            var Q8;
            Q8=makeQuery(id+"F5.opExtrude","CAP_FACE",FACE,{"disambiguationData":[OSD([sQuery(id+"F4.wireOp",EDGE,"E16.0.8.0"),sQuery(id+"F4.wireOp",EDGE,"E16.0.8.1"),sQuery(id+"F4.wireOp",EDGE,"E16.0.8.2"),sQuery(id+"F4.wireOp",EDGE,"E16.0.8.3")])],"isStart":false});
            var Q9;
            Q9=makeQuery(id+"F5.opExtrude","CAP_FACE",FACE,{"disambiguationData":[OSD([sQuery(id+"F4.wireOp",EDGE,"E16.0.9.0"),sQuery(id+"F4.wireOp",EDGE,"E16.0.9.1"),sQuery(id+"F4.wireOp",EDGE,"E16.0.9.2"),sQuery(id+"F4.wireOp",EDGE,"E16.0.9.3")])],"isStart":false});
            var Q10;
            Q10=makeQuery(id+"F5.opExtrude","CAP_FACE",FACE,{"disambiguationData":[OSD([sQuery(id+"F4.wireOp",EDGE,"E16.0.10.0"),sQuery(id+"F4.wireOp",EDGE,"E16.0.10.1"),sQuery(id+"F4.wireOp",EDGE,"E16.0.10.2"),sQuery(id+"F4.wireOp",EDGE,"E16.0.10.3")])],"isStart":false});
            var Q11;
            Q11=makeQuery(id+"F5.opExtrude","CAP_FACE",FACE,{"disambiguationData":[OSD([sQuery(id+"F4.wireOp",EDGE,"E16.0.11.0"),sQuery(id+"F4.wireOp",EDGE,"E16.0.11.1"),sQuery(id+"F4.wireOp",EDGE,"E16.0.11.2"),sQuery(id+"F4.wireOp",EDGE,"E16.0.11.3")])],"isStart":false});
            var Q12;
            Q12=makeQuery(id+"F5.opExtrude","CAP_FACE",FACE,{"disambiguationData":[OSD([sQuery(id+"F4.wireOp",EDGE,"E16.0.12.0"),sQuery(id+"F4.wireOp",EDGE,"E16.0.12.1"),sQuery(id+"F4.wireOp",EDGE,"E16.0.12.2"),sQuery(id+"F4.wireOp",EDGE,"E16.0.12.3")])],"isStart":false});
            var Q13;
            Q13=makeQuery(id+"F5.opExtrude","CAP_FACE",FACE,{"disambiguationData":[OSD([sQuery(id+"F4.wireOp",EDGE,"E16.0.13.0"),sQuery(id+"F4.wireOp",EDGE,"E16.0.13.1"),sQuery(id+"F4.wireOp",EDGE,"E16.0.13.2"),sQuery(id+"F4.wireOp",EDGE,"E16.0.13.3")])],"isStart":false});
            var Q14;
            Q14=makeQuery(id+"F5.opExtrude","CAP_FACE",FACE,{"disambiguationData":[OSD([sQuery(id+"F4.wireOp",EDGE,"E16.0.14.0"),sQuery(id+"F4.wireOp",EDGE,"E16.0.14.1"),sQuery(id+"F4.wireOp",EDGE,"E16.0.14.2"),sQuery(id+"F4.wireOp",EDGE,"E16.0.14.3")])],"isStart":false});
            var Q15;
            Q15=makeQuery(id+"F5.opExtrude","CAP_FACE",FACE,{"disambiguationData":[OSD([sQuery(id+"F4.wireOp",EDGE,"E16.0.15.0"),sQuery(id+"F4.wireOp",EDGE,"E16.0.15.1"),sQuery(id+"F4.wireOp",EDGE,"E16.0.15.2"),sQuery(id+"F4.wireOp",EDGE,"E16.0.15.3")])],"isStart":false});
            var Q16;
            Q16=makeQuery(id+"F5.opExtrude","CAP_FACE",FACE,{"disambiguationData":[OSD([sQuery(id+"F4.wireOp",EDGE,"E16.0.16.0"),sQuery(id+"F4.wireOp",EDGE,"E16.0.16.1"),sQuery(id+"F4.wireOp",EDGE,"E16.0.16.2"),sQuery(id+"F4.wireOp",EDGE,"E16.0.16.3")])],"isStart":false});
            var Q17;
            Q17=makeQuery(id+"F5.opExtrude","CAP_FACE",FACE,{"disambiguationData":[OSD([sQuery(id+"F4.wireOp",EDGE,"E16.0.17.0"),sQuery(id+"F4.wireOp",EDGE,"E16.0.17.1"),sQuery(id+"F4.wireOp",EDGE,"E16.0.17.2"),sQuery(id+"F4.wireOp",EDGE,"E16.0.17.3")])],"isStart":false});
            var Q18;
            Q18=makeQuery(id+"F5.opExtrude","CAP_FACE",FACE,{"disambiguationData":[OSD([sQuery(id+"F4.wireOp",EDGE,"E16.0.18.0"),sQuery(id+"F4.wireOp",EDGE,"E16.0.18.1"),sQuery(id+"F4.wireOp",EDGE,"E16.0.18.2"),sQuery(id+"F4.wireOp",EDGE,"E16.0.18.3")])],"isStart":false});
            var Q19;
            Q19=makeQuery(id+"F5.opExtrude","CAP_FACE",FACE,{"disambiguationData":[OSD([sQuery(id+"F4.wireOp",EDGE,"E16.0.19.0"),sQuery(id+"F4.wireOp",EDGE,"E16.0.19.1"),sQuery(id+"F4.wireOp",EDGE,"E16.0.19.2"),sQuery(id+"F4.wireOp",EDGE,"E16.0.19.3")])],"isStart":false});
            fillet(context, id + "F6", {"entities" : qUnion([Q0, Q1, Q2, Q3, Q4, Q5, Q6, Q7, Q8, Q9, Q10, Q11, Q12, Q13, Q14, Q15, Q16, Q17, Q18, Q19]), "radius" : 1 * mm, "tangentPropagation" : true, "allowEdgeOverflow" : false});
        }
    });
